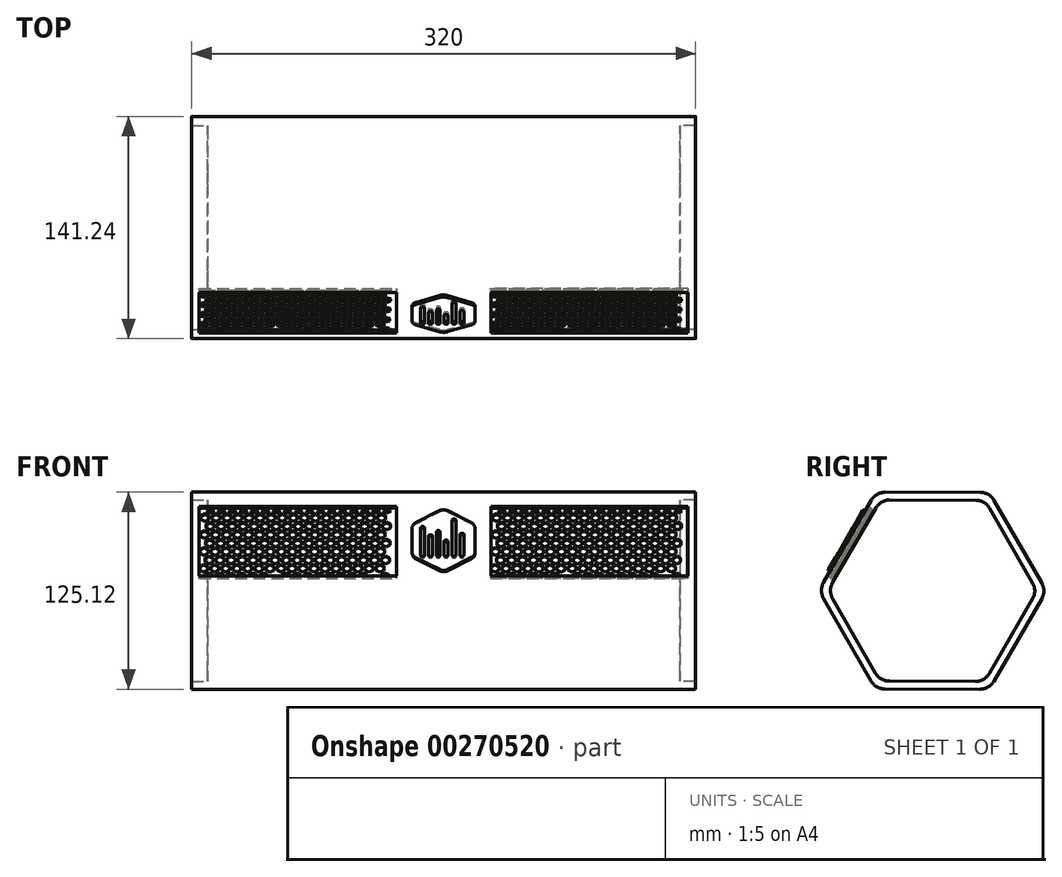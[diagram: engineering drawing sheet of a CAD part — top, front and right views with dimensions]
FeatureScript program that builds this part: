
annotation { "Feature Type Name" : "Feature", "Feature Type Description" : "" }
export const myFeature = defineFeature(function(context is Context, id is Id, definition is map)
    precondition{}
    {
        {
            var Q0;
            Q0=qCreatedBy(makeId("Right.planeOp"),FACE);
            var sketch = newSketch(context, id + "F0", { "sketchPlane" : qUnion([Q0])});
            skCircle(sketch, "E0.cCircle", {"center": v(0, 0) * mm, "radius": 62.5 * mm, "construction": true});
            skLineSegment(sketch, "E0.0", {"start": v(-72.17, 0.15) * mm, "end": v(-35.96, 62.57) * mm});
            skLineSegment(sketch, "E0.1", {"start": v(-35.96, 62.57) * mm, "end": v(36.21, 62.43) * mm});
            skLineSegment(sketch, "E0.2", {"start": v(36.21, 62.43) * mm, "end": v(72.17, -0.15) * mm});
            skLineSegment(sketch, "E0.3", {"start": v(72.17, -0.15) * mm, "end": v(35.96, -62.57) * mm});
            skLineSegment(sketch, "E0.4", {"start": v(35.96, -62.57) * mm, "end": v(-36.21, -62.43) * mm});
            skLineSegment(sketch, "E0.5", {"start": v(-36.21, -62.43) * mm, "end": v(-72.17, 0.15) * mm});
            skPoint(sketch, "E0.0.midPoint", {"position": v(-54.06, 31.36) * mm});
            skSolve(sketch);
        }
        {
            var Q0;
            Q0=makeQuery(id+"F0.imprint","IMPRINT",FACE,{"disambiguationData":[TD([[makeQuery(id+"F0.imprint","IMPRINT",EDGE,{"derivedFrom":sQuery(id+"F0.wireOp",EDGE,"E0.0")}),-1.0]])]});
            extrude(context, id + "F1", {"entities" : qUnion([Q0]), "depth" : 320 * mm});
        }
        {
            var Q0;
            Q0=makeQuery(id+"F1.opExtrude","SWEPT_FACE",FACE,{"disambiguationData":[OSD([sQuery(id+"F0.wireOp",EDGE,"E0.0")])]});
            var sketch = newSketch(context, id + "F2", { "sketchPlane" : qUnion([Q0])});
            skLineSegment(sketch, "E1", {"start": v(0, 0) * mm, "end": v(320, 0) * mm, "construction": true});
            skLineSegment(sketch, "E2", {"start": v(160, 36.08) * mm, "end": v(160, -36.08) * mm, "construction": true});
            skCircle(sketch, "E3.cCircle", {"center": v(160, 0) * mm, "radius": 19.98 * mm, "construction": true});
            skLineSegment(sketch, "E3.0", {"start": v(139.95, 11.4) * mm, "end": v(159.86, 23.07) * mm});
            skLineSegment(sketch, "E3.1", {"start": v(159.86, 23.07) * mm, "end": v(179.9, 11.66) * mm});
            skLineSegment(sketch, "E3.2", {"start": v(179.9, 11.66) * mm, "end": v(180.05, -11.4) * mm});
            skLineSegment(sketch, "E3.3", {"start": v(180.05, -11.4) * mm, "end": v(160.14, -23.07) * mm});
            skLineSegment(sketch, "E3.4", {"start": v(160.14, -23.07) * mm, "end": v(140.1, -11.66) * mm});
            skLineSegment(sketch, "E3.5", {"start": v(140.1, -11.66) * mm, "end": v(139.95, 11.4) * mm});
            skPoint(sketch, "E3.0.midPoint", {"position": v(149.9, 17.24) * mm});
            skSolve(sketch);
        }
        {
            var Q0;
            Q0=makeQuery(id+"F2.imprint","IMPRINT",FACE,{"disambiguationData":[TD([[makeQuery(id+"F2.imprint","IMPRINT",EDGE,{"derivedFrom":sQuery(id+"F2.wireOp",EDGE,"E3.0")}),-1.0]])]});
            extrude(context, id + "F3", {"entities" : qUnion([Q0]), "depth" : 1.5 * mm});
        }
        {
            var Q0;
            Q0=makeQuery(id+"F1.opExtrude","SWEPT_EDGE",EDGE,{"disambiguationData":[OSD([sQuery(id+"F0.wireOp",EDGE,"E0.1"),sQuery(id+"F0.wireOp",EDGE,"E0.2")])]});
            var Q1;
            Q1=makeQuery(id+"F1.opExtrude","SWEPT_EDGE",EDGE,{"disambiguationData":[OSD([sQuery(id+"F0.wireOp",EDGE,"E0.0"),sQuery(id+"F0.wireOp",EDGE,"E0.1")])]});
            var Q2;
            Q2=makeQuery(id+"F1.opExtrude","SWEPT_EDGE",EDGE,{"disambiguationData":[OSD([sQuery(id+"F0.wireOp",EDGE,"E0.0"),sQuery(id+"F0.wireOp",EDGE,"E0.5")])]});
            var Q3;
            Q3=makeQuery(id+"F1.opExtrude","SWEPT_EDGE",EDGE,{"disambiguationData":[OSD([sQuery(id+"F0.wireOp",EDGE,"E0.4"),sQuery(id+"F0.wireOp",EDGE,"E0.5")])]});
            var Q4;
            Q4=makeQuery(id+"F1.opExtrude","SWEPT_EDGE",EDGE,{"disambiguationData":[OSD([sQuery(id+"F0.wireOp",EDGE,"E0.3"),sQuery(id+"F0.wireOp",EDGE,"E0.4")])]});
            var Q5;
            Q5=makeQuery(id+"F1.opExtrude","SWEPT_EDGE",EDGE,{"disambiguationData":[OSD([sQuery(id+"F0.wireOp",EDGE,"E0.2"),sQuery(id+"F0.wireOp",EDGE,"E0.3")])]});
            fillet(context, id + "F4", {"entities" : qUnion([Q0, Q1, Q2, Q3, Q4, Q5]), "radius" : 10 * mm, "tangentPropagation" : true, "allowEdgeOverflow" : false});
        }
        {
            var Q0;
            Q0=makeQuery(id+"F1.opExtrude","CAP_FACE",FACE,{"disambiguationData":[OSD([sQuery(id+"F0.wireOp",EDGE,"E0.0"),sQuery(id+"F0.wireOp",EDGE,"E0.1"),sQuery(id+"F0.wireOp",EDGE,"E0.2"),sQuery(id+"F0.wireOp",EDGE,"E0.3"),sQuery(id+"F0.wireOp",EDGE,"E0.4"),sQuery(id+"F0.wireOp",EDGE,"E0.5")])],"isStart":true});
            var sketch = newSketch(context, id + "F5", { "sketchPlane" : qUnion([Q0])});
            skLineSegment(sketch, "E4", {"start": v(0, 62.5) * mm, "end": v(0.01, 57.5) * mm, "construction": true});
            skCircle(sketch, "E5.cCircle", {"center": v(0, 0) * mm, "radius": 57.5 * mm, "construction": true});
            skLineSegment(sketch, "E5.0", {"start": v(-33.19, 57.5) * mm, "end": v(33.2, 57.5) * mm});
            skLineSegment(sketch, "E5.1", {"start": v(33.2, 57.5) * mm, "end": v(66.4, -0.01) * mm});
            skLineSegment(sketch, "E5.2", {"start": v(66.4, -0.01) * mm, "end": v(33.19, -57.5) * mm});
            skLineSegment(sketch, "E5.3", {"start": v(33.19, -57.5) * mm, "end": v(-33.2, -57.5) * mm});
            skLineSegment(sketch, "E5.4", {"start": v(-33.2, -57.5) * mm, "end": v(-66.4, 0.01) * mm});
            skLineSegment(sketch, "E5.5", {"start": v(-66.4, 0.01) * mm, "end": v(-33.19, 57.5) * mm});
            skPoint(sketch, "E5.0.midPoint", {"position": v(0.01, 57.5) * mm});
            skSolve(sketch);
        }
        {
            var Q0;
            Q0=makeQuery(id+"F5.imprint","IMPRINT",FACE,{"disambiguationData":[TD([[makeQuery(id+"F5.imprint","IMPRINT",EDGE,{"derivedFrom":sQuery(id+"F5.wireOp",EDGE,"E5.0")}),-1.0]])]});
            extrude(context, id + "F6", {"entities" : qUnion([Q0]), "operationType" : NewBodyOperationType.REMOVE, "oppositeDirection" : true, "depth" : 10 * mm});
        }
        {
            var Q0;
            Q0=makeQuery(id+"F1.opExtrude","CAP_FACE",FACE,{"disambiguationData":[OSD([sQuery(id+"F0.wireOp",EDGE,"E0.0"),sQuery(id+"F0.wireOp",EDGE,"E0.1"),sQuery(id+"F0.wireOp",EDGE,"E0.2"),sQuery(id+"F0.wireOp",EDGE,"E0.3"),sQuery(id+"F0.wireOp",EDGE,"E0.4"),sQuery(id+"F0.wireOp",EDGE,"E0.5")])],"isStart":false});
            var sketch = newSketch(context, id + "F7", { "sketchPlane" : qUnion([Q0])});
            skLineSegment(sketch, "E6", {"start": v(0.13, 62.5) * mm, "end": v(0.13, 57.5) * mm, "construction": true});
            skCircle(sketch, "E7.cCircle", {"center": v(0, 0) * mm, "radius": 57.5 * mm, "construction": true});
            skLineSegment(sketch, "E7.0", {"start": v(-33.07, 57.57) * mm, "end": v(33.33, 57.43) * mm});
            skLineSegment(sketch, "E7.1", {"start": v(33.33, 57.43) * mm, "end": v(66.4, -0.15) * mm});
            skLineSegment(sketch, "E7.2", {"start": v(66.4, -0.15) * mm, "end": v(33.07, -57.57) * mm});
            skLineSegment(sketch, "E7.3", {"start": v(33.07, -57.57) * mm, "end": v(-33.33, -57.43) * mm});
            skLineSegment(sketch, "E7.4", {"start": v(-33.33, -57.43) * mm, "end": v(-66.4, 0.15) * mm});
            skLineSegment(sketch, "E7.5", {"start": v(-66.4, 0.15) * mm, "end": v(-33.07, 57.57) * mm});
            skPoint(sketch, "E7.0.midPoint", {"position": v(0.13, 57.5) * mm});
            skSolve(sketch);
        }
        {
            var Q0;
            Q0=makeQuery(id+"F7.imprint","IMPRINT",FACE,{"disambiguationData":[TD([[makeQuery(id+"F7.imprint","IMPRINT",EDGE,{"derivedFrom":sQuery(id+"F7.wireOp",EDGE,"E7.0")}),-1.0]])]});
            extrude(context, id + "F8", {"entities" : qUnion([Q0]), "operationType" : NewBodyOperationType.REMOVE, "oppositeDirection" : true, "depth" : 10 * mm});
        }
        {
            var Q0;
            Q0=makeQuery(id+"F6.boolean.opBoolean","COPY",EDGE,{"derivedFrom":makeQuery(id+"F6.opExtrude","SWEPT_EDGE",EDGE,{"disambiguationData":[OSD([sQuery(id+"F5.wireOp",EDGE,"E5.0"),sQuery(id+"F5.wireOp",EDGE,"E5.5")])]})});
            var Q1;
            Q1=makeQuery(id+"F6.boolean.opBoolean","COPY",EDGE,{"derivedFrom":makeQuery(id+"F6.opExtrude","SWEPT_EDGE",EDGE,{"disambiguationData":[OSD([sQuery(id+"F5.wireOp",EDGE,"E5.4"),sQuery(id+"F5.wireOp",EDGE,"E5.5")])]})});
            var Q2;
            Q2=makeQuery(id+"F6.boolean.opBoolean","COPY",EDGE,{"derivedFrom":makeQuery(id+"F6.opExtrude","SWEPT_EDGE",EDGE,{"disambiguationData":[OSD([sQuery(id+"F5.wireOp",EDGE,"E5.0"),sQuery(id+"F5.wireOp",EDGE,"E5.1")])]})});
            var Q3;
            Q3=makeQuery(id+"F6.boolean.opBoolean","COPY",EDGE,{"derivedFrom":makeQuery(id+"F6.opExtrude","SWEPT_EDGE",EDGE,{"disambiguationData":[OSD([sQuery(id+"F5.wireOp",EDGE,"E5.1"),sQuery(id+"F5.wireOp",EDGE,"E5.2")])]})});
            var Q4;
            Q4=makeQuery(id+"F6.boolean.opBoolean","COPY",EDGE,{"derivedFrom":makeQuery(id+"F6.opExtrude","SWEPT_EDGE",EDGE,{"disambiguationData":[OSD([sQuery(id+"F5.wireOp",EDGE,"E5.2"),sQuery(id+"F5.wireOp",EDGE,"E5.3")])]})});
            var Q5;
            Q5=makeQuery(id+"F6.boolean.opBoolean","COPY",EDGE,{"derivedFrom":makeQuery(id+"F6.opExtrude","SWEPT_EDGE",EDGE,{"disambiguationData":[OSD([sQuery(id+"F5.wireOp",EDGE,"E5.3"),sQuery(id+"F5.wireOp",EDGE,"E5.4")])]})});
            var Q6;
            Q6=makeQuery(id+"F8.boolean.opBoolean","COPY",EDGE,{"derivedFrom":makeQuery(id+"F8.opExtrude","SWEPT_EDGE",EDGE,{"disambiguationData":[OSD([sQuery(id+"F7.wireOp",EDGE,"E7.0"),sQuery(id+"F7.wireOp",EDGE,"E7.1")])]})});
            var Q7;
            Q7=makeQuery(id+"F8.boolean.opBoolean","COPY",EDGE,{"derivedFrom":makeQuery(id+"F8.opExtrude","SWEPT_EDGE",EDGE,{"disambiguationData":[OSD([sQuery(id+"F7.wireOp",EDGE,"E7.1"),sQuery(id+"F7.wireOp",EDGE,"E7.2")])]})});
            var Q8;
            Q8=makeQuery(id+"F8.boolean.opBoolean","COPY",EDGE,{"derivedFrom":makeQuery(id+"F8.opExtrude","SWEPT_EDGE",EDGE,{"disambiguationData":[OSD([sQuery(id+"F7.wireOp",EDGE,"E7.0"),sQuery(id+"F7.wireOp",EDGE,"E7.5")])]})});
            var Q9;
            Q9=makeQuery(id+"F8.boolean.opBoolean","COPY",EDGE,{"derivedFrom":makeQuery(id+"F8.opExtrude","SWEPT_EDGE",EDGE,{"disambiguationData":[OSD([sQuery(id+"F7.wireOp",EDGE,"E7.4"),sQuery(id+"F7.wireOp",EDGE,"E7.5")])]})});
            var Q10;
            Q10=makeQuery(id+"F8.boolean.opBoolean","COPY",EDGE,{"derivedFrom":makeQuery(id+"F8.opExtrude","SWEPT_EDGE",EDGE,{"disambiguationData":[OSD([sQuery(id+"F7.wireOp",EDGE,"E7.3"),sQuery(id+"F7.wireOp",EDGE,"E7.4")])]})});
            var Q11;
            Q11=makeQuery(id+"F8.boolean.opBoolean","COPY",EDGE,{"derivedFrom":makeQuery(id+"F8.opExtrude","SWEPT_EDGE",EDGE,{"disambiguationData":[OSD([sQuery(id+"F7.wireOp",EDGE,"E7.2"),sQuery(id+"F7.wireOp",EDGE,"E7.3")])]})});
            fillet(context, id + "F9", {"entities" : qUnion([Q0, Q1, Q2, Q3, Q4, Q5, Q6, Q7, Q8, Q9, Q10, Q11]), "radius" : 10 * mm, "tangentPropagation" : true, "allowEdgeOverflow" : false});
        }
        {
            var Q0;
            Q0=makeQuery(id+"F3.opExtrude","SWEPT_EDGE",EDGE,{"disambiguationData":[OSD([sQuery(id+"F2.wireOp",EDGE,"E3.0"),sQuery(id+"F2.wireOp",EDGE,"E3.1")])]});
            var Q1;
            Q1=makeQuery(id+"F3.opExtrude","SWEPT_EDGE",EDGE,{"disambiguationData":[OSD([sQuery(id+"F2.wireOp",EDGE,"E3.1"),sQuery(id+"F2.wireOp",EDGE,"E3.2")])]});
            var Q2;
            Q2=makeQuery(id+"F3.opExtrude","SWEPT_EDGE",EDGE,{"disambiguationData":[OSD([sQuery(id+"F2.wireOp",EDGE,"E3.2"),sQuery(id+"F2.wireOp",EDGE,"E3.3")])]});
            var Q3;
            Q3=makeQuery(id+"F3.opExtrude","SWEPT_EDGE",EDGE,{"disambiguationData":[OSD([sQuery(id+"F2.wireOp",EDGE,"E3.3"),sQuery(id+"F2.wireOp",EDGE,"E3.4")])]});
            var Q4;
            Q4=makeQuery(id+"F3.opExtrude","SWEPT_EDGE",EDGE,{"disambiguationData":[OSD([sQuery(id+"F2.wireOp",EDGE,"E3.4"),sQuery(id+"F2.wireOp",EDGE,"E3.5")])]});
            var Q5;
            Q5=makeQuery(id+"F3.opExtrude","SWEPT_EDGE",EDGE,{"disambiguationData":[OSD([sQuery(id+"F2.wireOp",EDGE,"E3.0"),sQuery(id+"F2.wireOp",EDGE,"E3.5")])]});
            fillet(context, id + "F10", {"entities" : qUnion([Q0, Q1, Q2, Q3, Q4, Q5]), "radius" : 5 * mm, "tangentPropagation" : true, "allowEdgeOverflow" : false});
        }
        {
            var Q0;
            Q0=makeQuery(id+"F2.imprint","IMPRINT",FACE,{"disambiguationData":[TD([[makeQuery(id+"F2.imprint","IMPRINT",EDGE,{"derivedFrom":sQuery(id+"F2.wireOp",EDGE,"E3.0")}),1.0]])]});
            var sketch = newSketch(context, id + "F11", { "sketchPlane" : qUnion([Q0])});
            skLineSegment(sketch, "E8.bottom", {"start": v(4.75, 25.56) * mm, "end": v(130, 25.56) * mm});
            skLineSegment(sketch, "E8.top", {"start": v(4.75, -25.56) * mm, "end": v(130, -25.56) * mm});
            skLineSegment(sketch, "E8.left", {"start": v(4.75, 25.56) * mm, "end": v(4.75, -25.56) * mm});
            skLineSegment(sketch, "E8.right", {"start": v(130, 25.56) * mm, "end": v(130, -25.56) * mm});
            skLineSegment(sketch, "E9.MirrorCS", {"start": v(315.25, 25.56) * mm, "end": v(190, 25.56) * mm});
            skLineSegment(sketch, "E10.MirrorCS", {"start": v(315.25, 25.56) * mm, "end": v(315.25, -25.56) * mm});
            skLineSegment(sketch, "E11.MirrorCS", {"start": v(315.25, -25.56) * mm, "end": v(190, -25.56) * mm});
            skLineSegment(sketch, "E12.MirrorCS", {"start": v(190, 25.56) * mm, "end": v(190, -25.56) * mm});
            skSolve(sketch);
        }
        {
            var Q0;
            Q0=makeQuery(id+"F11.imprint","IMPRINT",FACE,{"disambiguationData":[TD([[makeQuery(id+"F11.imprint","IMPRINT",EDGE,{"derivedFrom":sQuery(id+"F11.wireOp",EDGE,"E8.bottom")}),-1.0]])]});
            extrude(context, id + "F12", {"entities" : qUnion([Q0]), "operationType" : NewBodyOperationType.REMOVE, "oppositeDirection" : true, "depth" : 3 * mm});
        }
        {
            var Q0;
            Q0=makeQuery(id+"F11.imprint","IMPRINT",FACE,{"disambiguationData":[TD([[makeQuery(id+"F11.imprint","IMPRINT",EDGE,{"derivedFrom":sQuery(id+"F11.wireOp",EDGE,"E9.MirrorCS")}),1.0]])]});
            extrude(context, id + "F13", {"entities" : qUnion([Q0]), "operationType" : NewBodyOperationType.REMOVE, "oppositeDirection" : true, "depth" : 3 * mm});
        }
        {
            var Q0;
            Q0=makeQuery(id+"F12.boolean.opBoolean","COPY",FACE,{"derivedFrom":makeQuery(id+"F12.opExtrude","CAP_FACE",FACE,{"disambiguationData":[OSD([sQuery(id+"F11.wireOp",EDGE,"E8.bottom"),sQuery(id+"F11.wireOp",EDGE,"E8.top"),sQuery(id+"F11.wireOp",EDGE,"E8.left"),sQuery(id+"F11.wireOp",EDGE,"E8.right")])],"isStart":false})});
            extrude(context, id + "F14", {"entities" : qUnion([Q0]), "depth" : 1 * mm});
        }
        {
            var Q0;
            Q0=makeQuery(id+"F14.opExtrude","CAP_FACE",FACE,{"disambiguationData":[OSD([sQuery(id+"F11.wireOp",EDGE,"E8.bottom"),sQuery(id+"F11.wireOp",EDGE,"E8.top"),sQuery(id+"F11.wireOp",EDGE,"E8.left"),sQuery(id+"F11.wireOp",EDGE,"E8.right")])],"isStart":false});
            var sketch = newSketch(context, id + "F15", { "sketchPlane" : qUnion([Q0])});
            skLineSegment(sketch, "E13", {"start": v(67.38, 25.56) * mm, "end": v(67.38, -25.56) * mm, "construction": true});
            skCircle(sketch, "E14.cCircle", {"center": v(67.38, 0) * mm, "radius": 2.5 * mm, "construction": true});
            skLineSegment(sketch, "E14.0", {"start": v(69.87, 1.44) * mm, "end": v(69.88, -1.44) * mm});
            skLineSegment(sketch, "E14.1", {"start": v(69.87, -1.44) * mm, "end": v(67.38, -2.89) * mm});
            skLineSegment(sketch, "E14.2", {"start": v(67.38, -2.89) * mm, "end": v(64.88, -1.44) * mm});
            skLineSegment(sketch, "E14.3", {"start": v(64.88, -1.44) * mm, "end": v(64.87, 1.44) * mm});
            skLineSegment(sketch, "E14.4", {"start": v(64.88, 1.44) * mm, "end": v(67.37, 2.89) * mm});
            skLineSegment(sketch, "E14.5", {"start": v(67.37, 2.89) * mm, "end": v(69.87, 1.44) * mm});
            skCircle(sketch, "E15.cCircle", {"center": v(74.37, 0) * mm, "radius": 2.5 * mm, "construction": true});
            skLineSegment(sketch, "E15.0", {"start": v(71.85, 1.4) * mm, "end": v(74.32, 2.89) * mm});
            skLineSegment(sketch, "E15.1", {"start": v(74.32, 2.89) * mm, "end": v(76.85, 1.5) * mm});
            skLineSegment(sketch, "E15.2", {"start": v(76.85, 1.5) * mm, "end": v(76.9, -1.4) * mm});
            skLineSegment(sketch, "E15.3", {"start": v(76.9, -1.4) * mm, "end": v(74.43, -2.89) * mm});
            skLineSegment(sketch, "E15.4", {"start": v(74.43, -2.89) * mm, "end": v(71.9, -1.5) * mm});
            skLineSegment(sketch, "E15.5", {"start": v(71.9, -1.5) * mm, "end": v(71.85, 1.4) * mm});
            skCircle(sketch, "E16.cCircle", {"center": v(81.37, 0) * mm, "radius": 2.5 * mm, "construction": true});
            skLineSegment(sketch, "E16.0", {"start": v(78.87, 1.44) * mm, "end": v(81.37, 2.89) * mm});
            skLineSegment(sketch, "E16.1", {"start": v(81.37, 2.89) * mm, "end": v(83.87, 1.44) * mm});
            skLineSegment(sketch, "E16.2", {"start": v(83.87, 1.44) * mm, "end": v(83.87, -1.44) * mm});
            skLineSegment(sketch, "E16.3", {"start": v(83.87, -1.44) * mm, "end": v(81.37, -2.89) * mm});
            skLineSegment(sketch, "E16.4", {"start": v(81.37, -2.89) * mm, "end": v(78.87, -1.44) * mm});
            skLineSegment(sketch, "E16.5", {"start": v(78.87, -1.44) * mm, "end": v(78.87, 1.44) * mm});
            skCircle(sketch, "E17.cCircle", {"center": v(88.37, 0) * mm, "radius": 2.5 * mm, "construction": true});
            skLineSegment(sketch, "E17.0", {"start": v(85.87, 1.44) * mm, "end": v(88.37, 2.89) * mm});
            skLineSegment(sketch, "E17.1", {"start": v(88.37, 2.89) * mm, "end": v(90.87, 1.44) * mm});
            skLineSegment(sketch, "E17.2", {"start": v(90.87, 1.44) * mm, "end": v(90.87, -1.44) * mm});
            skLineSegment(sketch, "E17.3", {"start": v(90.87, -1.44) * mm, "end": v(88.37, -2.89) * mm});
            skLineSegment(sketch, "E17.4", {"start": v(88.37, -2.89) * mm, "end": v(85.87, -1.44) * mm});
            skLineSegment(sketch, "E17.5", {"start": v(85.87, -1.44) * mm, "end": v(85.87, 1.44) * mm});
            skCircle(sketch, "E18.cCircle", {"center": v(95.37, 0) * mm, "radius": 2.5 * mm, "construction": true});
            skLineSegment(sketch, "E18.0", {"start": v(92.87, 1.44) * mm, "end": v(95.37, 2.89) * mm});
            skLineSegment(sketch, "E18.1", {"start": v(95.37, 2.89) * mm, "end": v(97.87, 1.44) * mm});
            skLineSegment(sketch, "E18.2", {"start": v(97.87, 1.44) * mm, "end": v(97.87, -1.44) * mm});
            skLineSegment(sketch, "E18.3", {"start": v(97.87, -1.44) * mm, "end": v(95.37, -2.89) * mm});
            skLineSegment(sketch, "E18.4", {"start": v(95.37, -2.89) * mm, "end": v(92.87, -1.44) * mm});
            skLineSegment(sketch, "E18.5", {"start": v(92.87, -1.44) * mm, "end": v(92.87, 1.44) * mm});
            skCircle(sketch, "E19.cCircle", {"center": v(102.38, 0) * mm, "radius": 2.5 * mm, "construction": true});
            skLineSegment(sketch, "E19.0", {"start": v(99.88, 1.44) * mm, "end": v(102.38, 2.89) * mm});
            skLineSegment(sketch, "E19.1", {"start": v(102.38, 2.89) * mm, "end": v(104.88, 1.44) * mm});
            skLineSegment(sketch, "E19.2", {"start": v(104.88, 1.44) * mm, "end": v(104.88, -1.44) * mm});
            skLineSegment(sketch, "E19.3", {"start": v(104.88, -1.44) * mm, "end": v(102.38, -2.89) * mm});
            skLineSegment(sketch, "E19.4", {"start": v(102.38, -2.89) * mm, "end": v(99.88, -1.44) * mm});
            skLineSegment(sketch, "E19.5", {"start": v(99.88, -1.44) * mm, "end": v(99.88, 1.44) * mm});
            skCircle(sketch, "E20.cCircle", {"center": v(109.38, 0) * mm, "radius": 2.5 * mm, "construction": true});
            skLineSegment(sketch, "E20.0", {"start": v(106.88, 1.44) * mm, "end": v(109.38, 2.89) * mm});
            skLineSegment(sketch, "E20.1", {"start": v(109.38, 2.89) * mm, "end": v(111.88, 1.44) * mm});
            skLineSegment(sketch, "E20.2", {"start": v(111.88, 1.44) * mm, "end": v(111.88, -1.44) * mm});
            skLineSegment(sketch, "E20.3", {"start": v(111.88, -1.44) * mm, "end": v(109.38, -2.89) * mm});
            skLineSegment(sketch, "E20.4", {"start": v(109.38, -2.89) * mm, "end": v(106.88, -1.44) * mm});
            skLineSegment(sketch, "E20.5", {"start": v(106.88, -1.44) * mm, "end": v(106.88, 1.44) * mm});
            skCircle(sketch, "E21.cCircle", {"center": v(116.38, 0) * mm, "radius": 2.5 * mm, "construction": true});
            skLineSegment(sketch, "E21.0", {"start": v(113.88, 1.44) * mm, "end": v(116.38, 2.89) * mm});
            skLineSegment(sketch, "E21.1", {"start": v(116.38, 2.89) * mm, "end": v(118.88, 1.44) * mm});
            skLineSegment(sketch, "E21.2", {"start": v(118.88, 1.44) * mm, "end": v(118.88, -1.44) * mm});
            skLineSegment(sketch, "E21.3", {"start": v(118.88, -1.44) * mm, "end": v(116.38, -2.89) * mm});
            skLineSegment(sketch, "E21.4", {"start": v(116.38, -2.89) * mm, "end": v(113.88, -1.44) * mm});
            skLineSegment(sketch, "E21.5", {"start": v(113.88, -1.44) * mm, "end": v(113.88, 1.44) * mm});
            skCircle(sketch, "E22.cCircle", {"center": v(123.37, 0) * mm, "radius": 2.5 * mm, "construction": true});
            skLineSegment(sketch, "E22.0", {"start": v(120.88, 1.44) * mm, "end": v(123.38, 2.89) * mm});
            skLineSegment(sketch, "E22.1", {"start": v(123.38, 2.89) * mm, "end": v(125.88, 1.44) * mm});
            skLineSegment(sketch, "E22.2", {"start": v(125.88, 1.44) * mm, "end": v(125.87, -1.44) * mm});
            skLineSegment(sketch, "E22.3", {"start": v(125.87, -1.44) * mm, "end": v(123.37, -2.89) * mm});
            skLineSegment(sketch, "E22.4", {"start": v(123.37, -2.89) * mm, "end": v(120.87, -1.44) * mm});
            skLineSegment(sketch, "E22.5", {"start": v(120.87, -1.44) * mm, "end": v(120.88, 1.44) * mm});
            skLineSegment(sketch, "E23.MirrorCS", {"start": v(25.37, -2.89) * mm, "end": v(27.87, -1.44) * mm});
            skLineSegment(sketch, "E24.MirrorCS", {"start": v(20.87, 1.44) * mm, "end": v(18.37, 2.89) * mm});
            skLineSegment(sketch, "E25.MirrorCS", {"start": v(18.37, -2.89) * mm, "end": v(20.87, -1.44) * mm});
            skLineSegment(sketch, "E26.MirrorCS", {"start": v(32.37, -2.89) * mm, "end": v(34.87, -1.44) * mm});
            skLineSegment(sketch, "E27.MirrorCS", {"start": v(11.37, 2.89) * mm, "end": v(8.87, 1.44) * mm});
            skLineSegment(sketch, "E28.MirrorCS", {"start": v(46.38, 2.89) * mm, "end": v(43.88, 1.44) * mm});
            skCircle(sketch, "E29.MirrorC", {"center": v(25.37, 0) * mm, "radius": 2.5 * mm, "construction": true});
            skLineSegment(sketch, "E30.MirrorCS", {"start": v(18.37, 2.89) * mm, "end": v(15.87, 1.44) * mm});
            skLineSegment(sketch, "E31.MirrorCS", {"start": v(8.88, -1.44) * mm, "end": v(11.38, -2.89) * mm});
            skLineSegment(sketch, "E32.MirrorCS", {"start": v(27.87, 1.44) * mm, "end": v(25.37, 2.89) * mm});
            skLineSegment(sketch, "E33.MirrorCS", {"start": v(13.87, 1.44) * mm, "end": v(11.37, 2.89) * mm});
            skLineSegment(sketch, "E34.MirrorCS", {"start": v(34.87, 1.44) * mm, "end": v(32.37, 2.89) * mm});
            skLineSegment(sketch, "E35.MirrorCS", {"start": v(20.87, -1.44) * mm, "end": v(20.87, 1.44) * mm});
            skLineSegment(sketch, "E36.MirrorCS", {"start": v(29.87, 1.44) * mm, "end": v(29.87, -1.44) * mm});
            skLineSegment(sketch, "E37.MirrorCS", {"start": v(11.38, -2.89) * mm, "end": v(13.88, -1.44) * mm});
            skLineSegment(sketch, "E38.MirrorCS", {"start": v(15.87, -1.44) * mm, "end": v(18.37, -2.89) * mm});
            skLineSegment(sketch, "E39.MirrorCS", {"start": v(8.87, 1.44) * mm, "end": v(8.88, -1.44) * mm});
            skLineSegment(sketch, "E40.MirrorCS", {"start": v(53.38, -2.89) * mm, "end": v(55.88, -1.44) * mm});
            skLineSegment(sketch, "E41.MirrorCS", {"start": v(55.88, 1.44) * mm, "end": v(53.38, 2.89) * mm});
            skLineSegment(sketch, "E42.MirrorCS", {"start": v(22.87, -1.44) * mm, "end": v(25.37, -2.89) * mm});
            skCircle(sketch, "E43.MirrorC", {"center": v(18.37, 0) * mm, "radius": 2.5 * mm, "construction": true});
            skLineSegment(sketch, "E44.MirrorCS", {"start": v(41.88, 1.44) * mm, "end": v(39.38, 2.89) * mm});
            skLineSegment(sketch, "E45.MirrorCS", {"start": v(34.87, -1.44) * mm, "end": v(34.87, 1.44) * mm});
            skCircle(sketch, "E46.MirrorC", {"center": v(11.38, 0) * mm, "radius": 2.5 * mm, "construction": true});
            skLineSegment(sketch, "E47.MirrorCS", {"start": v(53.38, 2.89) * mm, "end": v(50.88, 1.44) * mm});
            skLineSegment(sketch, "E48.MirrorCS", {"start": v(32.37, 2.89) * mm, "end": v(29.87, 1.44) * mm});
            skLineSegment(sketch, "E49.MirrorCS", {"start": v(50.88, -1.44) * mm, "end": v(53.38, -2.89) * mm});
            skCircle(sketch, "E50.MirrorC", {"center": v(32.37, 0) * mm, "radius": 2.5 * mm, "construction": true});
            skLineSegment(sketch, "E51.MirrorCS", {"start": v(46.38, -2.89) * mm, "end": v(48.88, -1.44) * mm});
            skLineSegment(sketch, "E52.MirrorCS", {"start": v(48.88, 1.44) * mm, "end": v(46.38, 2.89) * mm});
            skLineSegment(sketch, "E53.MirrorCS", {"start": v(13.88, -1.44) * mm, "end": v(13.87, 1.44) * mm});
            skLineSegment(sketch, "E54.MirrorCS", {"start": v(39.38, 2.89) * mm, "end": v(36.88, 1.44) * mm});
            skLineSegment(sketch, "E55.MirrorCS", {"start": v(43.88, -1.44) * mm, "end": v(46.38, -2.89) * mm});
            skLineSegment(sketch, "E56.MirrorCS", {"start": v(29.87, -1.44) * mm, "end": v(32.37, -2.89) * mm});
            skLineSegment(sketch, "E57.MirrorCS", {"start": v(36.88, -1.44) * mm, "end": v(39.38, -2.89) * mm});
            skLineSegment(sketch, "E58.MirrorCS", {"start": v(39.38, -2.89) * mm, "end": v(41.88, -1.44) * mm});
            skLineSegment(sketch, "E59.MirrorCS", {"start": v(25.37, 2.89) * mm, "end": v(22.87, 1.44) * mm});
            skLineSegment(sketch, "E60.MirrorCS", {"start": v(22.87, 1.44) * mm, "end": v(22.87, -1.44) * mm});
            skLineSegment(sketch, "E61.MirrorCS", {"start": v(15.87, 1.44) * mm, "end": v(15.87, -1.44) * mm});
            skLineSegment(sketch, "E62.MirrorCS", {"start": v(27.87, -1.44) * mm, "end": v(27.87, 1.44) * mm});
            skLineSegment(sketch, "E63.MirrorCS", {"start": v(55.88, -1.44) * mm, "end": v(55.88, 1.44) * mm});
            skLineSegment(sketch, "E64.MirrorCS", {"start": v(36.88, 1.44) * mm, "end": v(36.88, -1.44) * mm});
            skLineSegment(sketch, "E65.MirrorCS", {"start": v(48.88, -1.44) * mm, "end": v(48.88, 1.44) * mm});
            skLineSegment(sketch, "E66.MirrorCS", {"start": v(43.88, 1.44) * mm, "end": v(43.88, -1.44) * mm});
            skLineSegment(sketch, "E67.MirrorCS", {"start": v(50.88, 1.44) * mm, "end": v(50.88, -1.44) * mm});
            skLineSegment(sketch, "E68.MirrorCS", {"start": v(41.88, -1.44) * mm, "end": v(41.88, 1.44) * mm});
            skCircle(sketch, "E69.MirrorC", {"center": v(53.38, 0) * mm, "radius": 2.5 * mm, "construction": true});
            skCircle(sketch, "E70.MirrorC", {"center": v(39.38, 0) * mm, "radius": 2.5 * mm, "construction": true});
            skCircle(sketch, "E71.MirrorC", {"center": v(46.38, 0) * mm, "radius": 2.5 * mm, "construction": true});
            skLineSegment(sketch, "E72.MirrorCS", {"start": v(60.43, 2.89) * mm, "end": v(57.9, 1.5) * mm});
            skLineSegment(sketch, "E73.MirrorCS", {"start": v(57.85, -1.4) * mm, "end": v(60.32, -2.89) * mm});
            skLineSegment(sketch, "E74.MirrorCS", {"start": v(62.85, -1.5) * mm, "end": v(62.9, 1.4) * mm});
            skLineSegment(sketch, "E75.MirrorCS", {"start": v(62.9, 1.4) * mm, "end": v(60.43, 2.89) * mm});
            skLineSegment(sketch, "E76.MirrorCS", {"start": v(57.9, 1.5) * mm, "end": v(57.85, -1.4) * mm});
            skLineSegment(sketch, "E77.MirrorCS", {"start": v(60.32, -2.89) * mm, "end": v(62.85, -1.5) * mm});
            skCircle(sketch, "E78.MirrorC", {"center": v(60.38, 0) * mm, "radius": 2.5 * mm, "construction": true});
            skCircle(sketch, "E79.1.0.4", {"center": v(36.24, 6.26) * mm, "radius": 2.5 * mm, "construction": true});
            skCircle(sketch, "E79.1.0.5", {"center": v(85.24, 6.26) * mm, "radius": 2.5 * mm, "construction": true});
            skCircle(sketch, "E79.1.0.6", {"center": v(64.24, 6.26) * mm, "radius": 2.5 * mm, "construction": true});
            skLineSegment(sketch, "E79.1.0.7", {"start": v(47.74, 7.7) * mm, "end": v(47.74, 4.82) * mm});
            skLineSegment(sketch, "E79.1.0.8", {"start": v(103.74, 7.7) * mm, "end": v(106.24, 9.15) * mm});
            skLineSegment(sketch, "E79.1.0.9", {"start": v(8.24, 3.37) * mm, "end": v(10.74, 4.82) * mm});
            skLineSegment(sketch, "E79.1.0.10", {"start": v(120.24, 3.37) * mm, "end": v(117.74, 4.82) * mm});
            skLineSegment(sketch, "E79.1.0.11", {"start": v(19.74, 7.7) * mm, "end": v(19.74, 4.82) * mm});
            skLineSegment(sketch, "E79.1.0.12", {"start": v(10.74, 4.82) * mm, "end": v(10.74, 7.7) * mm});
            skLineSegment(sketch, "E79.1.0.13", {"start": v(38.74, 7.7) * mm, "end": v(36.24, 9.15) * mm});
            skCircle(sketch, "E79.1.0.14", {"center": v(50.24, 6.26) * mm, "radius": 2.5 * mm, "construction": true});
            skLineSegment(sketch, "E79.1.0.15", {"start": v(89.74, 7.7) * mm, "end": v(92.24, 9.15) * mm});
            skLineSegment(sketch, "E79.1.0.16", {"start": v(96.74, 7.7) * mm, "end": v(99.24, 9.15) * mm});
            skLineSegment(sketch, "E79.1.0.17", {"start": v(66.74, 4.82) * mm, "end": v(64.24, 3.37) * mm});
            skLineSegment(sketch, "E79.1.0.18", {"start": v(115.74, 7.7) * mm, "end": v(115.74, 4.82) * mm});
            skLineSegment(sketch, "E79.1.0.19", {"start": v(108.74, 7.7) * mm, "end": v(108.74, 4.82) * mm});
            skLineSegment(sketch, "E79.1.0.20", {"start": v(40.74, 7.7) * mm, "end": v(40.74, 4.82) * mm});
            skCircle(sketch, "E79.1.0.21", {"center": v(106.24, 6.26) * mm, "radius": 2.5 * mm, "construction": true});
            skCircle(sketch, "E79.1.0.22", {"center": v(29.24, 6.26) * mm, "radius": 2.5 * mm, "construction": true});
            skLineSegment(sketch, "E79.1.0.23", {"start": v(85.24, 3.37) * mm, "end": v(82.74, 4.82) * mm});
            skCircle(sketch, "E79.1.0.24", {"center": v(15.24, 6.26) * mm, "radius": 2.5 * mm, "construction": true});
            skLineSegment(sketch, "E79.1.0.25", {"start": v(78.24, 3.37) * mm, "end": v(75.74, 4.82) * mm});
            skLineSegment(sketch, "E79.1.0.26", {"start": v(8.24, 9.15) * mm, "end": v(5.74, 7.7) * mm});
            skLineSegment(sketch, "E79.1.0.27", {"start": v(122.74, 4.82) * mm, "end": v(120.24, 3.37) * mm});
            skLineSegment(sketch, "E79.1.0.28", {"start": v(64.24, 3.37) * mm, "end": v(61.74, 4.82) * mm});
            skLineSegment(sketch, "E79.1.0.29", {"start": v(45.74, 7.7) * mm, "end": v(43.24, 9.15) * mm});
            skLineSegment(sketch, "E79.1.0.30", {"start": v(113.24, 9.15) * mm, "end": v(115.74, 7.7) * mm});
            skLineSegment(sketch, "E79.1.0.31", {"start": v(59.77, 7.65) * mm, "end": v(57.3, 9.15) * mm});
            skLineSegment(sketch, "E79.1.0.32", {"start": v(38.74, 4.82) * mm, "end": v(38.74, 7.7) * mm});
            skLineSegment(sketch, "E79.1.0.33", {"start": v(106.24, 9.15) * mm, "end": v(108.74, 7.7) * mm});
            skCircle(sketch, "E79.1.0.34", {"center": v(92.24, 6.26) * mm, "radius": 2.5 * mm, "construction": true});
            skCircle(sketch, "E79.1.0.35", {"center": v(99.24, 6.26) * mm, "radius": 2.5 * mm, "construction": true});
            skLineSegment(sketch, "E79.1.0.36", {"start": v(45.74, 4.82) * mm, "end": v(45.74, 7.7) * mm});
            skLineSegment(sketch, "E79.1.0.37", {"start": v(96.74, 4.82) * mm, "end": v(96.74, 7.7) * mm});
            skLineSegment(sketch, "E79.1.0.38", {"start": v(117.74, 7.7) * mm, "end": v(120.24, 9.15) * mm});
            skLineSegment(sketch, "E79.1.0.39", {"start": v(47.74, 4.82) * mm, "end": v(50.24, 3.37) * mm});
            skLineSegment(sketch, "E79.1.0.40", {"start": v(10.74, 7.7) * mm, "end": v(8.24, 9.15) * mm});
            skLineSegment(sketch, "E79.1.0.41", {"start": v(59.71, 4.77) * mm, "end": v(59.77, 7.65) * mm});
            skLineSegment(sketch, "E79.1.0.42", {"start": v(89.74, 4.82) * mm, "end": v(89.74, 7.7) * mm});
            skLineSegment(sketch, "E79.1.0.43", {"start": v(110.74, 7.7) * mm, "end": v(113.24, 9.15) * mm});
            skLineSegment(sketch, "E79.1.0.44", {"start": v(33.74, 4.82) * mm, "end": v(36.24, 3.37) * mm});
            skLineSegment(sketch, "E79.1.0.45", {"start": v(52.74, 7.7) * mm, "end": v(50.24, 9.15) * mm});
            skLineSegment(sketch, "E79.1.0.46", {"start": v(29.24, 3.37) * mm, "end": v(31.74, 4.82) * mm});
            skLineSegment(sketch, "E79.1.0.47", {"start": v(26.74, 4.82) * mm, "end": v(29.24, 3.37) * mm});
            skLineSegment(sketch, "E79.1.0.48", {"start": v(24.74, 4.82) * mm, "end": v(24.74, 7.7) * mm});
            skLineSegment(sketch, "E79.1.0.49", {"start": v(101.74, 7.7) * mm, "end": v(101.74, 4.82) * mm});
            skCircle(sketch, "E79.1.0.50", {"center": v(57.24, 6.26) * mm, "radius": 2.5 * mm, "construction": true});
            skLineSegment(sketch, "E79.1.0.51", {"start": v(113.24, 3.37) * mm, "end": v(110.74, 4.82) * mm});
            skLineSegment(sketch, "E79.1.0.52", {"start": v(15.24, 9.15) * mm, "end": v(12.74, 7.7) * mm});
            skCircle(sketch, "E79.1.0.53", {"center": v(8.24, 6.26) * mm, "radius": 2.5 * mm, "construction": true});
            skCircle(sketch, "E79.1.0.54", {"center": v(120.24, 6.26) * mm, "radius": 2.5 * mm, "construction": true});
            skLineSegment(sketch, "E79.1.0.55", {"start": v(24.74, 7.7) * mm, "end": v(22.24, 9.15) * mm});
            skLineSegment(sketch, "E79.1.0.56", {"start": v(5.74, 7.7) * mm, "end": v(5.74, 4.82) * mm});
            skLineSegment(sketch, "E79.1.0.57", {"start": v(87.74, 7.7) * mm, "end": v(87.74, 4.82) * mm});
            skLineSegment(sketch, "E79.1.0.58", {"start": v(29.24, 9.15) * mm, "end": v(26.74, 7.7) * mm});
            skCircle(sketch, "E79.1.0.59", {"center": v(43.24, 6.26) * mm, "radius": 2.5 * mm, "construction": true});
            skLineSegment(sketch, "E79.1.0.60", {"start": v(94.74, 7.7) * mm, "end": v(94.74, 4.82) * mm});
            skLineSegment(sketch, "E79.1.0.61", {"start": v(75.74, 7.7) * mm, "end": v(78.24, 9.15) * mm});
            skLineSegment(sketch, "E79.1.0.62", {"start": v(106.24, 3.37) * mm, "end": v(103.74, 4.82) * mm});
            skLineSegment(sketch, "E79.1.0.63", {"start": v(73.77, 4.87) * mm, "end": v(71.3, 3.37) * mm});
            skLineSegment(sketch, "E79.1.0.64", {"start": v(73.71, 7.75) * mm, "end": v(73.77, 4.87) * mm});
            skLineSegment(sketch, "E79.1.0.65", {"start": v(71.19, 9.15) * mm, "end": v(73.71, 7.75) * mm});
            skLineSegment(sketch, "E79.1.0.66", {"start": v(68.71, 7.65) * mm, "end": v(71.19, 9.15) * mm});
            skCircle(sketch, "E79.1.0.67", {"center": v(71.24, 6.26) * mm, "radius": 2.5 * mm, "construction": true});
            skLineSegment(sketch, "E79.1.0.68", {"start": v(64.24, 9.15) * mm, "end": v(66.74, 7.7) * mm});
            skLineSegment(sketch, "E79.1.0.69", {"start": v(117.74, 4.82) * mm, "end": v(117.74, 7.7) * mm});
            skLineSegment(sketch, "E79.1.0.70", {"start": v(36.24, 9.15) * mm, "end": v(33.74, 7.7) * mm});
            skLineSegment(sketch, "E79.1.0.71", {"start": v(31.74, 4.82) * mm, "end": v(31.74, 7.7) * mm});
            skLineSegment(sketch, "E79.1.0.72", {"start": v(57.19, 3.37) * mm, "end": v(59.71, 4.77) * mm});
            skLineSegment(sketch, "E79.1.0.73", {"start": v(61.74, 7.7) * mm, "end": v(64.24, 9.15) * mm});
            skLineSegment(sketch, "E79.1.0.74", {"start": v(92.24, 9.15) * mm, "end": v(94.74, 7.7) * mm});
            skLineSegment(sketch, "E79.1.0.75", {"start": v(108.74, 4.82) * mm, "end": v(106.24, 3.37) * mm});
            skLineSegment(sketch, "E79.1.0.76", {"start": v(120.24, 9.15) * mm, "end": v(122.74, 7.7) * mm});
            skLineSegment(sketch, "E79.1.0.77", {"start": v(17.74, 4.82) * mm, "end": v(17.74, 7.7) * mm});
            skLineSegment(sketch, "E79.1.0.78", {"start": v(122.74, 7.7) * mm, "end": v(122.74, 4.82) * mm});
            skLineSegment(sketch, "E79.1.0.79", {"start": v(92.24, 3.37) * mm, "end": v(89.74, 4.82) * mm});
            skLineSegment(sketch, "E79.1.0.80", {"start": v(82.74, 4.82) * mm, "end": v(82.74, 7.7) * mm});
            skCircle(sketch, "E79.1.0.81", {"center": v(78.24, 6.26) * mm, "radius": 2.5 * mm, "construction": true});
            skLineSegment(sketch, "E79.1.0.82", {"start": v(68.77, 4.77) * mm, "end": v(68.71, 7.65) * mm});
            skLineSegment(sketch, "E79.1.0.83", {"start": v(71.3, 3.37) * mm, "end": v(68.77, 4.77) * mm});
            skLineSegment(sketch, "E79.1.0.84", {"start": v(50.24, 3.37) * mm, "end": v(52.74, 4.82) * mm});
            skLineSegment(sketch, "E79.1.0.85", {"start": v(103.74, 4.82) * mm, "end": v(103.74, 7.7) * mm});
            skLineSegment(sketch, "E79.1.0.86", {"start": v(82.74, 7.7) * mm, "end": v(85.24, 9.15) * mm});
            skLineSegment(sketch, "E79.1.0.87", {"start": v(22.24, 3.37) * mm, "end": v(24.74, 4.82) * mm});
            skLineSegment(sketch, "E79.1.0.88", {"start": v(40.74, 4.82) * mm, "end": v(43.24, 3.37) * mm});
            skLineSegment(sketch, "E79.1.0.89", {"start": v(54.77, 7.75) * mm, "end": v(54.71, 4.87) * mm});
            skLineSegment(sketch, "E79.1.0.90", {"start": v(80.74, 7.7) * mm, "end": v(80.74, 4.82) * mm});
            skLineSegment(sketch, "E79.1.0.91", {"start": v(75.74, 4.82) * mm, "end": v(75.74, 7.7) * mm});
            skCircle(sketch, "E79.1.0.92", {"center": v(22.24, 6.26) * mm, "radius": 2.5 * mm, "construction": true});
            skLineSegment(sketch, "E79.1.0.93", {"start": v(87.74, 4.82) * mm, "end": v(85.24, 3.37) * mm});
            skLineSegment(sketch, "E79.1.0.94", {"start": v(36.24, 3.37) * mm, "end": v(38.74, 4.82) * mm});
            skLineSegment(sketch, "E79.1.0.95", {"start": v(33.74, 7.7) * mm, "end": v(33.74, 4.82) * mm});
            skLineSegment(sketch, "E79.1.0.96", {"start": v(99.24, 3.37) * mm, "end": v(96.74, 4.82) * mm});
            skCircle(sketch, "E79.1.0.97", {"center": v(113.24, 6.26) * mm, "radius": 2.5 * mm, "construction": true});
            skLineSegment(sketch, "E79.1.0.98", {"start": v(101.74, 4.82) * mm, "end": v(99.24, 3.37) * mm});
            skLineSegment(sketch, "E79.1.0.99", {"start": v(110.74, 4.82) * mm, "end": v(110.74, 7.7) * mm});
            skLineSegment(sketch, "E79.1.0.100", {"start": v(50.24, 9.15) * mm, "end": v(47.74, 7.7) * mm});
            skLineSegment(sketch, "E79.1.0.101", {"start": v(17.74, 7.7) * mm, "end": v(15.24, 9.15) * mm});
            skLineSegment(sketch, "E79.1.0.102", {"start": v(57.3, 9.15) * mm, "end": v(54.77, 7.75) * mm});
            skLineSegment(sketch, "E79.1.0.103", {"start": v(94.74, 4.82) * mm, "end": v(92.24, 3.37) * mm});
            skLineSegment(sketch, "E79.1.0.104", {"start": v(78.24, 9.15) * mm, "end": v(80.74, 7.7) * mm});
            skLineSegment(sketch, "E79.1.0.105", {"start": v(43.24, 9.15) * mm, "end": v(40.74, 7.7) * mm});
            skLineSegment(sketch, "E79.1.0.106", {"start": v(12.74, 4.82) * mm, "end": v(15.24, 3.37) * mm});
            skLineSegment(sketch, "E79.1.0.107", {"start": v(85.24, 9.15) * mm, "end": v(87.74, 7.7) * mm});
            skLineSegment(sketch, "E79.1.0.108", {"start": v(66.74, 7.7) * mm, "end": v(66.74, 4.82) * mm});
            skLineSegment(sketch, "E79.1.0.109", {"start": v(31.74, 7.7) * mm, "end": v(29.24, 9.15) * mm});
            skLineSegment(sketch, "E79.1.0.110", {"start": v(26.74, 7.7) * mm, "end": v(26.74, 4.82) * mm});
            skLineSegment(sketch, "E79.1.0.111", {"start": v(22.24, 9.15) * mm, "end": v(19.74, 7.7) * mm});
            skLineSegment(sketch, "E79.1.0.112", {"start": v(19.74, 4.82) * mm, "end": v(22.24, 3.37) * mm});
            skLineSegment(sketch, "E79.1.0.113", {"start": v(15.24, 3.37) * mm, "end": v(17.74, 4.82) * mm});
            skLineSegment(sketch, "E79.1.0.114", {"start": v(80.74, 4.82) * mm, "end": v(78.24, 3.37) * mm});
            skLineSegment(sketch, "E79.1.0.115", {"start": v(54.71, 4.87) * mm, "end": v(57.19, 3.37) * mm});
            skLineSegment(sketch, "E79.1.0.116", {"start": v(12.74, 7.7) * mm, "end": v(12.74, 4.82) * mm});
            skLineSegment(sketch, "E79.1.0.117", {"start": v(115.74, 4.82) * mm, "end": v(113.24, 3.37) * mm});
            skLineSegment(sketch, "E79.1.0.118", {"start": v(99.24, 9.15) * mm, "end": v(101.74, 7.7) * mm});
            skLineSegment(sketch, "E79.1.0.119", {"start": v(61.74, 4.82) * mm, "end": v(61.74, 7.7) * mm});
            skLineSegment(sketch, "E79.1.0.120", {"start": v(43.24, 3.37) * mm, "end": v(45.74, 4.82) * mm});
            skLineSegment(sketch, "E79.1.0.121", {"start": v(52.74, 4.82) * mm, "end": v(52.74, 7.7) * mm});
            skLineSegment(sketch, "E79.1.0.122", {"start": v(5.74, 4.82) * mm, "end": v(8.24, 3.37) * mm});
            skLineSegment(sketch, "E79.direction1", {"start": v(8.88, -1.44) * mm, "end": v(5.74, 4.82) * mm, "construction": true});
            skLineSegment(sketch, "E80.1.0.0", {"start": v(9.2, 10.99) * mm, "end": v(6.07, 17.25) * mm, "construction": true});
            skLineSegment(sketch, "E80.1.0.1", {"start": v(126.2, 10.99) * mm, "end": v(123.7, 9.54) * mm});
            skLineSegment(sketch, "E80.1.0.2", {"start": v(30.2, 13.87) * mm, "end": v(30.2, 10.99) * mm});
            skLineSegment(sketch, "E80.1.0.3", {"start": v(119.2, 10.99) * mm, "end": v(116.7, 9.54) * mm});
            skLineSegment(sketch, "E80.1.0.4", {"start": v(29.57, 15.8) * mm, "end": v(32.07, 17.25) * mm});
            skLineSegment(sketch, "E80.1.0.5", {"start": v(56.2, 13.87) * mm, "end": v(53.7, 15.32) * mm});
            skLineSegment(sketch, "E80.1.0.6", {"start": v(21.2, 10.99) * mm, "end": v(21.2, 13.87) * mm});
            skLineSegment(sketch, "E80.1.0.7", {"start": v(51.2, 10.99) * mm, "end": v(53.7, 9.54) * mm});
            skLineSegment(sketch, "E80.1.0.8", {"start": v(91.2, 10.99) * mm, "end": v(88.7, 9.54) * mm});
            skLineSegment(sketch, "E80.1.0.9", {"start": v(20.07, 20.13) * mm, "end": v(20.07, 17.25) * mm});
            skLineSegment(sketch, "E80.1.0.10", {"start": v(123.07, 17.25) * mm, "end": v(120.57, 15.8) * mm});
            skLineSegment(sketch, "E80.1.0.11", {"start": v(27.07, 20.13) * mm, "end": v(27.07, 17.25) * mm});
            skLineSegment(sketch, "E80.1.0.12", {"start": v(121.2, 10.99) * mm, "end": v(121.2, 13.87) * mm});
            skLineSegment(sketch, "E80.1.0.13", {"start": v(25.7, 9.54) * mm, "end": v(28.2, 10.99) * mm});
            skLineSegment(sketch, "E80.1.0.14", {"start": v(22.57, 21.58) * mm, "end": v(20.07, 20.13) * mm});
            skLineSegment(sketch, "E80.1.0.15", {"start": v(123.07, 20.13) * mm, "end": v(123.07, 17.25) * mm});
            skCircle(sketch, "E80.1.0.16", {"center": v(43.57, 18.69) * mm, "radius": 2.5 * mm, "construction": true});
            skLineSegment(sketch, "E80.1.0.17", {"start": v(37.2, 10.99) * mm, "end": v(39.7, 9.54) * mm});
            skLineSegment(sketch, "E80.1.0.18", {"start": v(49.2, 13.87) * mm, "end": v(46.7, 15.32) * mm});
            skLineSegment(sketch, "E80.1.0.19", {"start": v(9.2, 13.87) * mm, "end": v(9.2, 10.99) * mm});
            skCircle(sketch, "E80.1.0.20", {"center": v(46.7, 12.43) * mm, "radius": 2.5 * mm, "construction": true});
            skLineSegment(sketch, "E80.1.0.21", {"start": v(44.2, 10.99) * mm, "end": v(46.7, 9.54) * mm});
            skLineSegment(sketch, "E80.1.0.22", {"start": v(32.07, 17.25) * mm, "end": v(32.07, 20.13) * mm});
            skLineSegment(sketch, "E80.1.0.23", {"start": v(44.2, 13.87) * mm, "end": v(44.2, 10.99) * mm});
            skLineSegment(sketch, "E80.1.0.24", {"start": v(85.57, 15.8) * mm, "end": v(83.07, 17.25) * mm});
            skLineSegment(sketch, "E80.1.0.25", {"start": v(79.2, 13.87) * mm, "end": v(81.7, 15.32) * mm});
            skLineSegment(sketch, "E80.1.0.26", {"start": v(16.2, 10.99) * mm, "end": v(18.7, 9.54) * mm});
            skLineSegment(sketch, "E80.1.0.27", {"start": v(119.2, 13.87) * mm, "end": v(119.2, 10.99) * mm});
            skCircle(sketch, "E80.1.0.28", {"center": v(18.7, 12.43) * mm, "radius": 2.5 * mm, "construction": true});
            skLineSegment(sketch, "E80.1.0.29", {"start": v(81.7, 9.54) * mm, "end": v(79.2, 10.99) * mm});
            skLineSegment(sketch, "E80.1.0.30", {"start": v(58.23, 13.92) * mm, "end": v(58.18, 11.04) * mm});
            skLineSegment(sketch, "E80.1.0.31", {"start": v(23.2, 13.87) * mm, "end": v(23.2, 10.99) * mm});
            skLineSegment(sketch, "E80.1.0.32", {"start": v(79.2, 10.99) * mm, "end": v(79.2, 13.87) * mm});
            skLineSegment(sketch, "E80.1.0.33", {"start": v(46.7, 15.32) * mm, "end": v(44.2, 13.87) * mm});
            skCircle(sketch, "E80.1.0.34", {"center": v(39.7, 12.43) * mm, "radius": 2.5 * mm, "construction": true});
            skLineSegment(sketch, "E80.1.0.35", {"start": v(42.2, 13.87) * mm, "end": v(39.7, 15.32) * mm});
            skLineSegment(sketch, "E80.1.0.36", {"start": v(71.52, 21.58) * mm, "end": v(74.04, 20.18) * mm});
            skLineSegment(sketch, "E80.1.0.37", {"start": v(53.07, 17.25) * mm, "end": v(53.07, 20.13) * mm});
            skLineSegment(sketch, "E80.1.0.38", {"start": v(67.7, 9.54) * mm, "end": v(65.2, 10.99) * mm});
            skCircle(sketch, "E80.1.0.39", {"center": v(67.7, 12.43) * mm, "radius": 2.5 * mm, "construction": true});
            skCircle(sketch, "E80.1.0.40", {"center": v(120.57, 18.69) * mm, "radius": 2.5 * mm, "construction": true});
            skCircle(sketch, "E80.1.0.41", {"center": v(81.7, 12.43) * mm, "radius": 2.5 * mm, "construction": true});
            skLineSegment(sketch, "E80.1.0.42", {"start": v(83.07, 20.13) * mm, "end": v(85.57, 21.58) * mm});
            skLineSegment(sketch, "E80.1.0.43", {"start": v(14.2, 13.87) * mm, "end": v(11.7, 15.32) * mm});
            skLineSegment(sketch, "E80.1.0.44", {"start": v(121.2, 13.87) * mm, "end": v(123.7, 15.32) * mm});
            skLineSegment(sketch, "E80.1.0.45", {"start": v(109.07, 20.13) * mm, "end": v(109.07, 17.25) * mm});
            skCircle(sketch, "E80.1.0.46", {"center": v(99.57, 18.69) * mm, "radius": 2.5 * mm, "construction": true});
            skCircle(sketch, "E80.1.0.47", {"center": v(116.7, 12.43) * mm, "radius": 2.5 * mm, "construction": true});
            skLineSegment(sketch, "E80.1.0.48", {"start": v(114.2, 10.99) * mm, "end": v(114.2, 13.87) * mm});
            skLineSegment(sketch, "E80.1.0.49", {"start": v(53.7, 15.32) * mm, "end": v(51.2, 13.87) * mm});
            skLineSegment(sketch, "E80.1.0.50", {"start": v(105.2, 10.99) * mm, "end": v(102.7, 9.54) * mm});
            skLineSegment(sketch, "E80.1.0.51", {"start": v(41.07, 20.13) * mm, "end": v(41.07, 17.25) * mm});
            skCircle(sketch, "E80.1.0.52", {"center": v(36.57, 18.69) * mm, "radius": 2.5 * mm, "construction": true});
            skLineSegment(sketch, "E80.1.0.53", {"start": v(109.7, 15.32) * mm, "end": v(112.2, 13.87) * mm});
            skLineSegment(sketch, "E80.1.0.54", {"start": v(56.2, 10.99) * mm, "end": v(56.2, 13.87) * mm});
            skLineSegment(sketch, "E80.1.0.55", {"start": v(50.57, 21.58) * mm, "end": v(48.07, 20.13) * mm});
            skLineSegment(sketch, "E80.1.0.56", {"start": v(50.57, 15.8) * mm, "end": v(53.07, 17.25) * mm});
            skLineSegment(sketch, "E80.1.0.57", {"start": v(64.57, 21.58) * mm, "end": v(67.07, 20.13) * mm});
            skLineSegment(sketch, "E80.1.0.58", {"start": v(15.57, 21.58) * mm, "end": v(13.07, 20.13) * mm});
            skLineSegment(sketch, "E80.1.0.59", {"start": v(58.18, 11.04) * mm, "end": v(60.65, 9.54) * mm});
            skLineSegment(sketch, "E80.1.0.60", {"start": v(112.2, 10.99) * mm, "end": v(109.7, 9.54) * mm});
            skLineSegment(sketch, "E80.1.0.61", {"start": v(95.7, 15.32) * mm, "end": v(98.2, 13.87) * mm});
            skLineSegment(sketch, "E80.1.0.62", {"start": v(95.7, 9.54) * mm, "end": v(93.2, 10.99) * mm});
            skLineSegment(sketch, "E80.1.0.63", {"start": v(88.7, 9.54) * mm, "end": v(86.2, 10.99) * mm});
            skCircle(sketch, "E80.1.0.64", {"center": v(32.7, 12.43) * mm, "radius": 2.5 * mm, "construction": true});
            skLineSegment(sketch, "E80.1.0.65", {"start": v(123.7, 15.32) * mm, "end": v(126.2, 13.87) * mm});
            skLineSegment(sketch, "E80.1.0.66", {"start": v(35.2, 13.87) * mm, "end": v(32.7, 15.32) * mm});
            skCircle(sketch, "E80.1.0.67", {"center": v(109.7, 12.43) * mm, "radius": 2.5 * mm, "construction": true});
            skLineSegment(sketch, "E80.1.0.68", {"start": v(48.07, 17.25) * mm, "end": v(50.57, 15.8) * mm});
            skLineSegment(sketch, "E80.1.0.69", {"start": v(48.07, 20.13) * mm, "end": v(48.07, 17.25) * mm});
            skLineSegment(sketch, "E80.1.0.70", {"start": v(22.57, 15.8) * mm, "end": v(25.07, 17.25) * mm});
            skLineSegment(sketch, "E80.1.0.71", {"start": v(95.07, 17.25) * mm, "end": v(92.57, 15.8) * mm});
            skLineSegment(sketch, "E80.1.0.72", {"start": v(112.2, 13.87) * mm, "end": v(112.2, 10.99) * mm});
            skLineSegment(sketch, "E80.1.0.73", {"start": v(14.2, 10.99) * mm, "end": v(14.2, 13.87) * mm});
            skLineSegment(sketch, "E80.1.0.74", {"start": v(123.7, 9.54) * mm, "end": v(121.2, 10.99) * mm});
            skLineSegment(sketch, "E80.1.0.75", {"start": v(29.57, 21.58) * mm, "end": v(27.07, 20.13) * mm});
            skLineSegment(sketch, "E80.1.0.76", {"start": v(74.76, 9.54) * mm, "end": v(72.23, 10.94) * mm});
            skLineSegment(sketch, "E80.1.0.77", {"start": v(74.65, 15.32) * mm, "end": v(77.18, 13.92) * mm});
            skLineSegment(sketch, "E80.1.0.78", {"start": v(91.2, 13.87) * mm, "end": v(91.2, 10.99) * mm});
            skLineSegment(sketch, "E80.1.0.79", {"start": v(72.18, 13.82) * mm, "end": v(74.65, 15.32) * mm});
            skLineSegment(sketch, "E80.1.0.80", {"start": v(57.52, 15.8) * mm, "end": v(60.04, 17.2) * mm});
            skCircle(sketch, "E80.1.0.81", {"center": v(64.57, 18.69) * mm, "radius": 2.5 * mm, "construction": true});
            skLineSegment(sketch, "E80.1.0.82", {"start": v(43.57, 15.8) * mm, "end": v(46.07, 17.25) * mm});
            skLineSegment(sketch, "E80.1.0.83", {"start": v(90.07, 17.25) * mm, "end": v(90.07, 20.13) * mm});
            skLineSegment(sketch, "E80.1.0.84", {"start": v(13.07, 20.13) * mm, "end": v(13.07, 17.25) * mm});
            skLineSegment(sketch, "E80.1.0.85", {"start": v(69.1, 17.2) * mm, "end": v(69.04, 20.08) * mm});
            skLineSegment(sketch, "E80.1.0.86", {"start": v(78.57, 21.58) * mm, "end": v(81.07, 20.13) * mm});
            skLineSegment(sketch, "E80.1.0.87", {"start": v(6.07, 20.13) * mm, "end": v(6.07, 17.25) * mm});
            skCircle(sketch, "E80.1.0.88", {"center": v(29.57, 18.69) * mm, "radius": 2.5 * mm, "construction": true});
            skLineSegment(sketch, "E80.1.0.89", {"start": v(104.07, 20.13) * mm, "end": v(106.57, 21.58) * mm});
            skLineSegment(sketch, "E80.1.0.90", {"start": v(41.07, 17.25) * mm, "end": v(43.57, 15.8) * mm});
            skLineSegment(sketch, "E80.1.0.91", {"start": v(126.2, 13.87) * mm, "end": v(126.2, 10.99) * mm});
            skLineSegment(sketch, "E80.1.0.92", {"start": v(18.7, 15.32) * mm, "end": v(16.2, 13.87) * mm});
            skLineSegment(sketch, "E80.1.0.93", {"start": v(86.2, 13.87) * mm, "end": v(88.7, 15.32) * mm});
            skCircle(sketch, "E80.1.0.94", {"center": v(95.7, 12.43) * mm, "radius": 2.5 * mm, "construction": true});
            skLineSegment(sketch, "E80.1.0.95", {"start": v(116.7, 9.54) * mm, "end": v(114.2, 10.99) * mm});
            skCircle(sketch, "E80.1.0.96", {"center": v(74.7, 12.43) * mm, "radius": 2.5 * mm, "construction": true});
            skLineSegment(sketch, "E80.1.0.97", {"start": v(120.57, 15.8) * mm, "end": v(118.07, 17.25) * mm});
            skLineSegment(sketch, "E80.1.0.98", {"start": v(88.7, 15.32) * mm, "end": v(91.2, 13.87) * mm});
            skLineSegment(sketch, "E80.1.0.99", {"start": v(11.07, 17.25) * mm, "end": v(11.07, 20.13) * mm});
            skCircle(sketch, "E80.1.0.100", {"center": v(102.7, 12.43) * mm, "radius": 2.5 * mm, "construction": true});
            skLineSegment(sketch, "E80.1.0.101", {"start": v(97.07, 20.13) * mm, "end": v(99.57, 21.58) * mm});
            skLineSegment(sketch, "E80.1.0.102", {"start": v(39.07, 17.25) * mm, "end": v(39.07, 20.13) * mm});
            skLineSegment(sketch, "E80.1.0.103", {"start": v(25.07, 17.25) * mm, "end": v(25.07, 20.13) * mm});
            skLineSegment(sketch, "E80.1.0.104", {"start": v(74.04, 20.18) * mm, "end": v(74.1, 17.3) * mm});
            skCircle(sketch, "E80.1.0.105", {"center": v(11.7, 12.43) * mm, "radius": 2.5 * mm, "construction": true});
            skLineSegment(sketch, "E80.1.0.106", {"start": v(107.2, 13.87) * mm, "end": v(109.7, 15.32) * mm});
            skLineSegment(sketch, "E80.1.0.107", {"start": v(36.57, 15.8) * mm, "end": v(39.07, 17.25) * mm});
            skLineSegment(sketch, "E80.1.0.108", {"start": v(25.7, 15.32) * mm, "end": v(23.2, 13.87) * mm});
            skLineSegment(sketch, "E80.1.0.109", {"start": v(11.7, 15.32) * mm, "end": v(9.2, 13.87) * mm});
            skLineSegment(sketch, "E80.1.0.110", {"start": v(63.23, 13.82) * mm, "end": v(60.76, 15.32) * mm});
            skLineSegment(sketch, "E80.1.0.111", {"start": v(105.2, 13.87) * mm, "end": v(105.2, 10.99) * mm});
            skLineSegment(sketch, "E80.1.0.112", {"start": v(116.7, 15.32) * mm, "end": v(119.2, 13.87) * mm});
            skLineSegment(sketch, "E80.1.0.113", {"start": v(98.2, 13.87) * mm, "end": v(98.2, 10.99) * mm});
            skLineSegment(sketch, "E80.1.0.114", {"start": v(32.07, 20.13) * mm, "end": v(29.57, 21.58) * mm});
            skCircle(sketch, "E80.1.0.115", {"center": v(50.57, 18.69) * mm, "radius": 2.5 * mm, "construction": true});
            skLineSegment(sketch, "E80.1.0.116", {"start": v(46.07, 20.13) * mm, "end": v(43.57, 21.58) * mm});
            skLineSegment(sketch, "E80.1.0.117", {"start": v(102.07, 17.25) * mm, "end": v(99.57, 15.8) * mm});
            skLineSegment(sketch, "E80.1.0.118", {"start": v(106.57, 15.8) * mm, "end": v(104.07, 17.25) * mm});
            skLineSegment(sketch, "E80.1.0.119", {"start": v(113.57, 15.8) * mm, "end": v(111.07, 17.25) * mm});
            skLineSegment(sketch, "E80.1.0.120", {"start": v(71.63, 15.8) * mm, "end": v(69.1, 17.2) * mm});
            skLineSegment(sketch, "E80.1.0.121", {"start": v(116.07, 17.25) * mm, "end": v(113.57, 15.8) * mm});
            skLineSegment(sketch, "E80.1.0.122", {"start": v(104.07, 17.25) * mm, "end": v(104.07, 20.13) * mm});
            skLineSegment(sketch, "E80.1.0.123", {"start": v(11.7, 9.54) * mm, "end": v(14.2, 10.99) * mm});
            skCircle(sketch, "E80.1.0.124", {"center": v(53.7, 12.43) * mm, "radius": 2.5 * mm, "construction": true});
            skLineSegment(sketch, "E80.1.0.125", {"start": v(93.2, 13.87) * mm, "end": v(95.7, 15.32) * mm});
            skLineSegment(sketch, "E80.1.0.126", {"start": v(62.07, 17.25) * mm, "end": v(62.07, 20.13) * mm});
            skLineSegment(sketch, "E80.1.0.127", {"start": v(25.07, 20.13) * mm, "end": v(22.57, 21.58) * mm});
            skLineSegment(sketch, "E80.1.0.128", {"start": v(67.07, 20.13) * mm, "end": v(67.07, 17.25) * mm});
            skLineSegment(sketch, "E80.1.0.129", {"start": v(64.57, 15.8) * mm, "end": v(62.07, 17.25) * mm});
            skCircle(sketch, "E80.1.0.130", {"center": v(22.57, 18.69) * mm, "radius": 2.5 * mm, "construction": true});
            skLineSegment(sketch, "E80.1.0.131", {"start": v(120.57, 21.58) * mm, "end": v(123.07, 20.13) * mm});
            skCircle(sketch, "E80.1.0.132", {"center": v(60.7, 12.43) * mm, "radius": 2.5 * mm, "construction": true});
            skLineSegment(sketch, "E80.1.0.133", {"start": v(111.07, 17.25) * mm, "end": v(111.07, 20.13) * mm});
            skCircle(sketch, "E80.1.0.134", {"center": v(71.57, 18.69) * mm, "radius": 2.5 * mm, "construction": true});
            skLineSegment(sketch, "E80.1.0.135", {"start": v(6.07, 17.25) * mm, "end": v(8.57, 15.8) * mm});
            skLineSegment(sketch, "E80.1.0.136", {"start": v(85.57, 21.58) * mm, "end": v(88.07, 20.13) * mm});
            skLineSegment(sketch, "E80.1.0.137", {"start": v(100.2, 10.99) * mm, "end": v(100.2, 13.87) * mm});
            skLineSegment(sketch, "E80.1.0.138", {"start": v(53.7, 9.54) * mm, "end": v(56.2, 10.99) * mm});
            skLineSegment(sketch, "E80.1.0.139", {"start": v(39.07, 20.13) * mm, "end": v(36.57, 21.58) * mm});
            skLineSegment(sketch, "E80.1.0.140", {"start": v(81.07, 17.25) * mm, "end": v(78.57, 15.8) * mm});
            skLineSegment(sketch, "E80.1.0.141", {"start": v(99.57, 15.8) * mm, "end": v(97.07, 17.25) * mm});
            skLineSegment(sketch, "E80.1.0.142", {"start": v(83.07, 17.25) * mm, "end": v(83.07, 20.13) * mm});
            skLineSegment(sketch, "E80.1.0.143", {"start": v(20.07, 17.25) * mm, "end": v(22.57, 15.8) * mm});
            skCircle(sketch, "E80.1.0.144", {"center": v(15.57, 18.69) * mm, "radius": 2.5 * mm, "construction": true});
            skLineSegment(sketch, "E80.1.0.145", {"start": v(67.7, 15.32) * mm, "end": v(70.2, 13.87) * mm});
            skLineSegment(sketch, "E80.1.0.146", {"start": v(116.07, 20.13) * mm, "end": v(116.07, 17.25) * mm});
            skLineSegment(sketch, "E80.1.0.147", {"start": v(18.07, 20.13) * mm, "end": v(15.57, 21.58) * mm});
            skCircle(sketch, "E80.1.0.148", {"center": v(8.57, 18.69) * mm, "radius": 2.5 * mm, "construction": true});
            skLineSegment(sketch, "E80.1.0.149", {"start": v(118.07, 17.25) * mm, "end": v(118.07, 20.13) * mm});
            skCircle(sketch, "E80.1.0.150", {"center": v(92.57, 18.69) * mm, "radius": 2.5 * mm, "construction": true});
            skLineSegment(sketch, "E80.1.0.151", {"start": v(55.04, 17.3) * mm, "end": v(57.52, 15.8) * mm});
            skLineSegment(sketch, "E80.1.0.152", {"start": v(86.2, 10.99) * mm, "end": v(86.2, 13.87) * mm});
            skLineSegment(sketch, "E80.1.0.153", {"start": v(42.2, 10.99) * mm, "end": v(42.2, 13.87) * mm});
            skLineSegment(sketch, "E80.1.0.154", {"start": v(77.23, 11.04) * mm, "end": v(74.76, 9.54) * mm});
            skLineSegment(sketch, "E80.1.0.155", {"start": v(46.7, 9.54) * mm, "end": v(49.2, 10.99) * mm});
            skCircle(sketch, "E80.1.0.156", {"center": v(25.7, 12.43) * mm, "radius": 2.5 * mm, "construction": true});
            skLineSegment(sketch, "E80.1.0.157", {"start": v(77.18, 13.92) * mm, "end": v(77.23, 11.04) * mm});
            skLineSegment(sketch, "E80.1.0.158", {"start": v(36.57, 21.58) * mm, "end": v(34.07, 20.13) * mm});
            skLineSegment(sketch, "E80.1.0.159", {"start": v(99.57, 21.58) * mm, "end": v(102.07, 20.13) * mm});
            skCircle(sketch, "E80.1.0.160", {"center": v(85.57, 18.69) * mm, "radius": 2.5 * mm, "construction": true});
            skLineSegment(sketch, "E80.1.0.161", {"start": v(13.07, 17.25) * mm, "end": v(15.57, 15.8) * mm});
            skCircle(sketch, "E80.1.0.162", {"center": v(106.57, 18.69) * mm, "radius": 2.5 * mm, "construction": true});
            skLineSegment(sketch, "E80.1.0.163", {"start": v(97.07, 17.25) * mm, "end": v(97.07, 20.13) * mm});
            skLineSegment(sketch, "E80.1.0.164", {"start": v(102.7, 9.54) * mm, "end": v(100.2, 10.99) * mm});
            skLineSegment(sketch, "E80.1.0.165", {"start": v(37.2, 13.87) * mm, "end": v(37.2, 10.99) * mm});
            skCircle(sketch, "E80.1.0.166", {"center": v(123.7, 12.43) * mm, "radius": 2.5 * mm, "construction": true});
            skLineSegment(sketch, "E80.1.0.167", {"start": v(114.2, 13.87) * mm, "end": v(116.7, 15.32) * mm});
            skLineSegment(sketch, "E80.1.0.168", {"start": v(81.07, 20.13) * mm, "end": v(81.07, 17.25) * mm});
            skLineSegment(sketch, "E80.1.0.169", {"start": v(93.2, 10.99) * mm, "end": v(93.2, 13.87) * mm});
            skLineSegment(sketch, "E80.1.0.170", {"start": v(84.2, 10.99) * mm, "end": v(81.7, 9.54) * mm});
            skLineSegment(sketch, "E80.1.0.171", {"start": v(39.7, 9.54) * mm, "end": v(42.2, 10.99) * mm});
            skLineSegment(sketch, "E80.1.0.172", {"start": v(23.2, 10.99) * mm, "end": v(25.7, 9.54) * mm});
            skCircle(sketch, "E80.1.0.173", {"center": v(57.57, 18.69) * mm, "radius": 2.5 * mm, "construction": true});
            skLineSegment(sketch, "E80.1.0.174", {"start": v(35.2, 10.99) * mm, "end": v(35.2, 13.87) * mm});
            skLineSegment(sketch, "E80.1.0.175", {"start": v(92.57, 21.58) * mm, "end": v(95.07, 20.13) * mm});
            skLineSegment(sketch, "E80.1.0.176", {"start": v(32.7, 9.54) * mm, "end": v(35.2, 10.99) * mm});
            skLineSegment(sketch, "E80.1.0.177", {"start": v(65.2, 13.87) * mm, "end": v(67.7, 15.32) * mm});
            skLineSegment(sketch, "E80.1.0.178", {"start": v(60.65, 9.54) * mm, "end": v(63.18, 10.94) * mm});
            skLineSegment(sketch, "E80.1.0.179", {"start": v(74.1, 17.3) * mm, "end": v(71.63, 15.8) * mm});
            skLineSegment(sketch, "E80.1.0.180", {"start": v(16.2, 13.87) * mm, "end": v(16.2, 10.99) * mm});
            skLineSegment(sketch, "E80.1.0.181", {"start": v(118.07, 20.13) * mm, "end": v(120.57, 21.58) * mm});
            skLineSegment(sketch, "E80.1.0.182", {"start": v(60.1, 20.08) * mm, "end": v(57.63, 21.58) * mm});
            skLineSegment(sketch, "E80.1.0.183", {"start": v(88.07, 17.25) * mm, "end": v(85.57, 15.8) * mm});
            skCircle(sketch, "E80.1.0.184", {"center": v(88.7, 12.43) * mm, "radius": 2.5 * mm, "construction": true});
            skLineSegment(sketch, "E80.1.0.185", {"start": v(27.07, 17.25) * mm, "end": v(29.57, 15.8) * mm});
            skLineSegment(sketch, "E80.1.0.186", {"start": v(51.2, 13.87) * mm, "end": v(51.2, 10.99) * mm});
            skLineSegment(sketch, "E80.1.0.187", {"start": v(43.57, 21.58) * mm, "end": v(41.07, 20.13) * mm});
            skLineSegment(sketch, "E80.1.0.188", {"start": v(102.7, 15.32) * mm, "end": v(105.2, 13.87) * mm});
            skLineSegment(sketch, "E80.1.0.189", {"start": v(55.1, 20.18) * mm, "end": v(55.04, 17.3) * mm});
            skLineSegment(sketch, "E80.1.0.190", {"start": v(65.2, 10.99) * mm, "end": v(65.2, 13.87) * mm});
            skLineSegment(sketch, "E80.1.0.191", {"start": v(90.07, 20.13) * mm, "end": v(92.57, 21.58) * mm});
            skLineSegment(sketch, "E80.1.0.192", {"start": v(92.57, 15.8) * mm, "end": v(90.07, 17.25) * mm});
            skLineSegment(sketch, "E80.1.0.193", {"start": v(70.2, 10.99) * mm, "end": v(67.7, 9.54) * mm});
            skLineSegment(sketch, "E80.1.0.194", {"start": v(8.57, 15.8) * mm, "end": v(11.07, 17.25) * mm});
            skLineSegment(sketch, "E80.1.0.195", {"start": v(28.2, 13.87) * mm, "end": v(25.7, 15.32) * mm});
            skCircle(sketch, "E80.1.0.196", {"center": v(78.57, 18.69) * mm, "radius": 2.5 * mm, "construction": true});
            skLineSegment(sketch, "E80.1.0.197", {"start": v(15.57, 15.8) * mm, "end": v(18.07, 17.25) * mm});
            skLineSegment(sketch, "E80.1.0.198", {"start": v(106.57, 21.58) * mm, "end": v(109.07, 20.13) * mm});
            skCircle(sketch, "E80.1.0.199", {"center": v(113.57, 18.69) * mm, "radius": 2.5 * mm, "construction": true});
            skLineSegment(sketch, "E80.1.0.200", {"start": v(67.07, 17.25) * mm, "end": v(64.57, 15.8) * mm});
            skLineSegment(sketch, "E80.1.0.201", {"start": v(102.07, 20.13) * mm, "end": v(102.07, 17.25) * mm});
            skLineSegment(sketch, "E80.1.0.202", {"start": v(34.07, 17.25) * mm, "end": v(36.57, 15.8) * mm});
            skLineSegment(sketch, "E80.1.0.203", {"start": v(95.07, 20.13) * mm, "end": v(95.07, 17.25) * mm});
            skLineSegment(sketch, "E80.1.0.204", {"start": v(57.63, 21.58) * mm, "end": v(55.1, 20.18) * mm});
            skLineSegment(sketch, "E80.1.0.205", {"start": v(109.07, 17.25) * mm, "end": v(106.57, 15.8) * mm});
            skLineSegment(sketch, "E80.1.0.206", {"start": v(76.07, 17.25) * mm, "end": v(76.07, 20.13) * mm});
            skLineSegment(sketch, "E80.1.0.207", {"start": v(107.2, 10.99) * mm, "end": v(107.2, 13.87) * mm});
            skLineSegment(sketch, "E80.1.0.208", {"start": v(98.2, 10.99) * mm, "end": v(95.7, 9.54) * mm});
            skLineSegment(sketch, "E80.1.0.209", {"start": v(81.7, 15.32) * mm, "end": v(84.2, 13.87) * mm});
            skLineSegment(sketch, "E80.1.0.210", {"start": v(60.76, 15.32) * mm, "end": v(58.23, 13.92) * mm});
            skLineSegment(sketch, "E80.1.0.211", {"start": v(21.2, 13.87) * mm, "end": v(18.7, 15.32) * mm});
            skLineSegment(sketch, "E80.1.0.212", {"start": v(30.2, 10.99) * mm, "end": v(32.7, 9.54) * mm});
            skLineSegment(sketch, "E80.1.0.213", {"start": v(53.07, 20.13) * mm, "end": v(50.57, 21.58) * mm});
            skLineSegment(sketch, "E80.1.0.214", {"start": v(76.07, 20.13) * mm, "end": v(78.57, 21.58) * mm});
            skLineSegment(sketch, "E80.1.0.215", {"start": v(111.07, 20.13) * mm, "end": v(113.57, 21.58) * mm});
            skLineSegment(sketch, "E80.1.0.216", {"start": v(72.23, 10.94) * mm, "end": v(72.18, 13.82) * mm});
            skLineSegment(sketch, "E80.1.0.217", {"start": v(39.7, 15.32) * mm, "end": v(37.2, 13.87) * mm});
            skLineSegment(sketch, "E80.1.0.218", {"start": v(78.57, 15.8) * mm, "end": v(76.07, 17.25) * mm});
            skLineSegment(sketch, "E80.1.0.219", {"start": v(60.04, 17.2) * mm, "end": v(60.1, 20.08) * mm});
            skLineSegment(sketch, "E80.1.0.220", {"start": v(88.07, 20.13) * mm, "end": v(88.07, 17.25) * mm});
            skLineSegment(sketch, "E80.1.0.221", {"start": v(18.07, 17.25) * mm, "end": v(18.07, 20.13) * mm});
            skLineSegment(sketch, "E80.1.0.222", {"start": v(100.2, 13.87) * mm, "end": v(102.7, 15.32) * mm});
            skLineSegment(sketch, "E80.1.0.223", {"start": v(62.07, 20.13) * mm, "end": v(64.57, 21.58) * mm});
            skLineSegment(sketch, "E80.1.0.224", {"start": v(9.2, 10.99) * mm, "end": v(11.7, 9.54) * mm});
            skLineSegment(sketch, "E80.1.0.225", {"start": v(46.07, 17.25) * mm, "end": v(46.07, 20.13) * mm});
            skLineSegment(sketch, "E80.1.0.226", {"start": v(109.7, 9.54) * mm, "end": v(107.2, 10.99) * mm});
            skLineSegment(sketch, "E80.1.0.227", {"start": v(84.2, 13.87) * mm, "end": v(84.2, 10.99) * mm});
            skLineSegment(sketch, "E80.1.0.228", {"start": v(8.57, 21.58) * mm, "end": v(6.07, 20.13) * mm});
            skLineSegment(sketch, "E80.1.0.229", {"start": v(11.07, 20.13) * mm, "end": v(8.57, 21.58) * mm});
            skLineSegment(sketch, "E80.1.0.230", {"start": v(113.57, 21.58) * mm, "end": v(116.07, 20.13) * mm});
            skLineSegment(sketch, "E80.1.0.231", {"start": v(18.7, 9.54) * mm, "end": v(21.2, 10.99) * mm});
            skLineSegment(sketch, "E80.1.0.232", {"start": v(28.2, 10.99) * mm, "end": v(28.2, 13.87) * mm});
            skLineSegment(sketch, "E80.1.0.233", {"start": v(63.18, 10.94) * mm, "end": v(63.23, 13.82) * mm});
            skLineSegment(sketch, "E80.1.0.234", {"start": v(69.04, 20.08) * mm, "end": v(71.52, 21.58) * mm});
            skLineSegment(sketch, "E80.1.0.235", {"start": v(34.07, 20.13) * mm, "end": v(34.07, 17.25) * mm});
            skLineSegment(sketch, "E80.1.0.236", {"start": v(70.2, 13.87) * mm, "end": v(70.2, 10.99) * mm});
            skLineSegment(sketch, "E80.1.0.237", {"start": v(32.7, 15.32) * mm, "end": v(30.2, 13.87) * mm});
            skLineSegment(sketch, "E80.1.0.238", {"start": v(49.2, 10.99) * mm, "end": v(49.2, 13.87) * mm});
            skLineSegment(sketch, "E80.2.0.1", {"start": v(126.53, 23.42) * mm, "end": v(124.03, 21.97) * mm});
            skLineSegment(sketch, "E80.2.0.3", {"start": v(119.53, 23.42) * mm, "end": v(117.03, 21.97) * mm});
            skLineSegment(sketch, "E80.2.0.7", {"start": v(51.53, 23.42) * mm, "end": v(54.03, 21.97) * mm});
            skLineSegment(sketch, "E80.2.0.8", {"start": v(91.53, 23.42) * mm, "end": v(89.03, 21.97) * mm});
            skLineSegment(sketch, "E80.2.0.13", {"start": v(26.03, 21.97) * mm, "end": v(28.53, 23.42) * mm});
            skLineSegment(sketch, "E80.2.0.17", {"start": v(37.53, 23.42) * mm, "end": v(40.03, 21.97) * mm});
            skLineSegment(sketch, "E80.2.0.21", {"start": v(44.53, 23.42) * mm, "end": v(47.03, 21.97) * mm});
            skLineSegment(sketch, "E80.2.0.26", {"start": v(16.53, 23.42) * mm, "end": v(19.03, 21.97) * mm});
            skLineSegment(sketch, "E80.2.0.29", {"start": v(82.03, 21.97) * mm, "end": v(79.53, 23.42) * mm});
            skLineSegment(sketch, "E80.2.0.38", {"start": v(68.03, 21.97) * mm, "end": v(65.53, 23.42) * mm});
            skLineSegment(sketch, "E80.2.0.50", {"start": v(105.53, 23.42) * mm, "end": v(103.03, 21.97) * mm});
            skLineSegment(sketch, "E80.2.0.59", {"start": v(58.5, 23.47) * mm, "end": v(60.98, 21.97) * mm});
            skLineSegment(sketch, "E80.2.0.60", {"start": v(112.53, 23.42) * mm, "end": v(110.03, 21.97) * mm});
            skLineSegment(sketch, "E80.2.0.62", {"start": v(96.03, 21.97) * mm, "end": v(93.53, 23.42) * mm});
            skLineSegment(sketch, "E80.2.0.63", {"start": v(89.03, 21.97) * mm, "end": v(86.53, 23.42) * mm});
            skLineSegment(sketch, "E80.2.0.74", {"start": v(124.03, 21.97) * mm, "end": v(121.53, 23.42) * mm});
            skLineSegment(sketch, "E80.2.0.76", {"start": v(75.1, 21.97) * mm, "end": v(72.56, 23.37) * mm});
            skLineSegment(sketch, "E80.2.0.95", {"start": v(117.03, 21.97) * mm, "end": v(114.53, 23.42) * mm});
            skLineSegment(sketch, "E80.2.0.123", {"start": v(12.03, 21.97) * mm, "end": v(14.53, 23.42) * mm});
            skLineSegment(sketch, "E80.2.0.138", {"start": v(54.03, 21.97) * mm, "end": v(56.53, 23.42) * mm});
            skLineSegment(sketch, "E80.2.0.154", {"start": v(77.56, 23.47) * mm, "end": v(75.1, 21.97) * mm});
            skLineSegment(sketch, "E80.2.0.155", {"start": v(47.03, 21.97) * mm, "end": v(49.53, 23.42) * mm});
            skLineSegment(sketch, "E80.2.0.164", {"start": v(103.03, 21.97) * mm, "end": v(100.53, 23.42) * mm});
            skLineSegment(sketch, "E80.2.0.170", {"start": v(84.53, 23.42) * mm, "end": v(82.03, 21.97) * mm});
            skLineSegment(sketch, "E80.2.0.171", {"start": v(40.03, 21.97) * mm, "end": v(42.53, 23.42) * mm});
            skLineSegment(sketch, "E80.2.0.172", {"start": v(23.53, 23.42) * mm, "end": v(26.03, 21.97) * mm});
            skLineSegment(sketch, "E80.2.0.176", {"start": v(33.03, 21.97) * mm, "end": v(35.53, 23.42) * mm});
            skLineSegment(sketch, "E80.2.0.178", {"start": v(60.98, 21.97) * mm, "end": v(63.5, 23.37) * mm});
            skLineSegment(sketch, "E80.2.0.193", {"start": v(70.53, 23.42) * mm, "end": v(68.03, 21.97) * mm});
            skLineSegment(sketch, "E80.2.0.208", {"start": v(98.53, 23.42) * mm, "end": v(96.03, 21.97) * mm});
            skLineSegment(sketch, "E80.2.0.212", {"start": v(30.53, 23.42) * mm, "end": v(33.03, 21.97) * mm});
            skLineSegment(sketch, "E80.2.0.224", {"start": v(9.53, 23.42) * mm, "end": v(12.03, 21.97) * mm});
            skLineSegment(sketch, "E80.2.0.226", {"start": v(110.03, 21.97) * mm, "end": v(107.53, 23.42) * mm});
            skLineSegment(sketch, "E80.2.0.231", {"start": v(19.03, 21.97) * mm, "end": v(21.53, 23.42) * mm});
            skLineSegment(sketch, "E80.direction1", {"start": v(8.88, -1.44) * mm, "end": v(9.2, 10.99) * mm, "construction": true});
            skLineSegment(sketch, "E81.1.0.0", {"start": v(24.47, -4.73) * mm, "end": v(21.97, -3.28) * mm});
            skLineSegment(sketch, "E81.1.0.1", {"start": v(75.47, -4.73) * mm, "end": v(77.97, -3.28) * mm});
            skLineSegment(sketch, "E81.1.0.2", {"start": v(54.44, -7.57) * mm, "end": v(56.91, -9.06) * mm});
            skLineSegment(sketch, "E81.1.0.3", {"start": v(48.6, -13.87) * mm, "end": v(48.6, -10.99) * mm});
            skLineSegment(sketch, "E81.1.0.4", {"start": v(20.6, -10.99) * mm, "end": v(18.1, -9.54) * mm});
            skCircle(sketch, "E81.1.0.5", {"center": v(35.97, -6.17) * mm, "radius": 2.5 * mm, "construction": true});
            skLineSegment(sketch, "E81.1.0.6", {"start": v(53.1, -15.32) * mm, "end": v(55.6, -13.87) * mm});
            skCircle(sketch, "E81.1.0.7", {"center": v(63.97, -6.17) * mm, "radius": 2.5 * mm, "construction": true});
            skLineSegment(sketch, "E81.1.0.8", {"start": v(20.6, -13.87) * mm, "end": v(20.6, -10.99) * mm});
            skCircle(sketch, "E81.1.0.9", {"center": v(28.97, -6.17) * mm, "radius": 2.5 * mm, "construction": true});
            skCircle(sketch, "E81.1.0.10", {"center": v(70.97, -6.17) * mm, "radius": 2.5 * mm, "construction": true});
            skLineSegment(sketch, "E81.1.0.11", {"start": v(110.47, -7.61) * mm, "end": v(110.47, -4.73) * mm});
            skLineSegment(sketch, "E81.1.0.12", {"start": v(61.47, -7.61) * mm, "end": v(61.47, -4.73) * mm});
            skLineSegment(sketch, "E81.1.0.13", {"start": v(94.47, -4.73) * mm, "end": v(94.47, -7.61) * mm});
            skLineSegment(sketch, "E81.1.0.14", {"start": v(5.47, -4.73) * mm, "end": v(5.47, -7.61) * mm});
            skLineSegment(sketch, "E81.1.0.15", {"start": v(8.6, -13.87) * mm, "end": v(5.47, -7.61) * mm, "construction": true});
            skLineSegment(sketch, "E81.1.0.16", {"start": v(56.91, -9.06) * mm, "end": v(59.44, -7.66) * mm});
            skCircle(sketch, "E81.1.0.17", {"center": v(11.1, -12.43) * mm, "radius": 2.5 * mm, "construction": true});
            skLineSegment(sketch, "E81.1.0.18", {"start": v(40.47, -7.61) * mm, "end": v(42.97, -9.06) * mm});
            skLineSegment(sketch, "E81.1.0.19", {"start": v(103.47, -4.73) * mm, "end": v(105.97, -3.28) * mm});
            skCircle(sketch, "E81.1.0.20", {"center": v(14.97, -6.17) * mm, "radius": 2.5 * mm, "construction": true});
            skLineSegment(sketch, "E81.1.0.21", {"start": v(76.63, -13.83) * mm, "end": v(74.16, -15.32) * mm});
            skLineSegment(sketch, "E81.1.0.22", {"start": v(102.1, -15.32) * mm, "end": v(99.6, -13.87) * mm});
            skCircle(sketch, "E81.1.0.23", {"center": v(109.1, -12.43) * mm, "radius": 2.5 * mm, "construction": true});
            skLineSegment(sketch, "E81.1.0.24", {"start": v(73.44, -4.68) * mm, "end": v(73.5, -7.57) * mm});
            skLineSegment(sketch, "E81.1.0.25", {"start": v(46.1, -15.32) * mm, "end": v(48.6, -13.87) * mm});
            skCircle(sketch, "E81.1.0.26", {"center": v(84.97, -6.17) * mm, "radius": 2.5 * mm, "construction": true});
            skLineSegment(sketch, "E81.1.0.27", {"start": v(21.97, -3.28) * mm, "end": v(19.47, -4.73) * mm});
            skCircle(sketch, "E81.1.0.28", {"center": v(105.97, -6.17) * mm, "radius": 2.5 * mm, "construction": true});
            skLineSegment(sketch, "E81.1.0.29", {"start": v(42.97, -9.06) * mm, "end": v(45.47, -7.61) * mm});
            skLineSegment(sketch, "E81.1.0.30", {"start": v(36.6, -10.99) * mm, "end": v(36.6, -13.87) * mm});
            skCircle(sketch, "E81.1.0.31", {"center": v(74.1, -12.43) * mm, "radius": 2.5 * mm, "construction": true});
            skLineSegment(sketch, "E81.1.0.32", {"start": v(64.6, -10.99) * mm, "end": v(67.1, -9.54) * mm});
            skLineSegment(sketch, "E81.1.0.33", {"start": v(64.6, -13.87) * mm, "end": v(64.6, -10.99) * mm});
            skCircle(sketch, "E81.1.0.34", {"center": v(91.97, -6.17) * mm, "radius": 2.5 * mm, "construction": true});
            skCircle(sketch, "E81.1.0.35", {"center": v(56.97, -6.17) * mm, "radius": 2.5 * mm, "construction": true});
            skCircle(sketch, "E81.1.0.36", {"center": v(25.1, -12.43) * mm, "radius": 2.5 * mm, "construction": true});
            skLineSegment(sketch, "E81.1.0.37", {"start": v(15.6, -10.99) * mm, "end": v(15.6, -13.87) * mm});
            skLineSegment(sketch, "E81.1.0.38", {"start": v(34.6, -13.87) * mm, "end": v(34.6, -10.99) * mm});
            skLineSegment(sketch, "E81.1.0.39", {"start": v(60.05, -15.32) * mm, "end": v(62.57, -13.92) * mm});
            skCircle(sketch, "E81.1.0.40", {"center": v(88.1, -12.43) * mm, "radius": 2.5 * mm, "construction": true});
            skLineSegment(sketch, "E81.1.0.41", {"start": v(11.1, -9.54) * mm, "end": v(8.6, -10.99) * mm});
            skCircle(sketch, "E81.1.0.42", {"center": v(46.1, -12.43) * mm, "radius": 2.5 * mm, "construction": true});
            skLineSegment(sketch, "E81.1.0.43", {"start": v(99.6, -13.87) * mm, "end": v(99.6, -10.99) * mm});
            skLineSegment(sketch, "E81.1.0.44", {"start": v(49.97, -3.28) * mm, "end": v(47.47, -4.73) * mm});
            skLineSegment(sketch, "E81.1.0.45", {"start": v(115.47, -7.61) * mm, "end": v(112.97, -9.06) * mm});
            skLineSegment(sketch, "E81.1.0.46", {"start": v(19.47, -7.61) * mm, "end": v(21.97, -9.06) * mm});
            skLineSegment(sketch, "E81.1.0.47", {"start": v(119.97, -3.28) * mm, "end": v(122.47, -4.73) * mm});
            skLineSegment(sketch, "E81.1.0.48", {"start": v(21.97, -9.06) * mm, "end": v(24.47, -7.61) * mm});
            skLineSegment(sketch, "E81.1.0.49", {"start": v(122.47, -4.73) * mm, "end": v(122.47, -7.61) * mm});
            skLineSegment(sketch, "E81.1.0.50", {"start": v(29.6, -13.87) * mm, "end": v(32.1, -15.32) * mm});
            skCircle(sketch, "E81.1.0.51", {"center": v(18.1, -12.43) * mm, "radius": 2.5 * mm, "construction": true});
            skLineSegment(sketch, "E81.1.0.52", {"start": v(57.63, -10.94) * mm, "end": v(57.57, -13.83) * mm});
            skCircle(sketch, "E81.1.0.53", {"center": v(81.1, -12.43) * mm, "radius": 2.5 * mm, "construction": true});
            skCircle(sketch, "E81.1.0.54", {"center": v(21.97, -6.17) * mm, "radius": 2.5 * mm, "construction": true});
            skLineSegment(sketch, "E81.1.0.55", {"start": v(55.6, -13.87) * mm, "end": v(55.6, -10.99) * mm});
            skLineSegment(sketch, "E81.1.0.56", {"start": v(27.6, -10.99) * mm, "end": v(25.1, -9.54) * mm});
            skCircle(sketch, "E81.1.0.57", {"center": v(123.1, -12.43) * mm, "radius": 2.5 * mm, "construction": true});
            skCircle(sketch, "E81.1.0.58", {"center": v(7.97, -6.17) * mm, "radius": 2.5 * mm, "construction": true});
            skLineSegment(sketch, "E81.1.0.59", {"start": v(22.6, -10.99) * mm, "end": v(22.6, -13.87) * mm});
            skLineSegment(sketch, "E81.1.0.60", {"start": v(57.03, -3.29) * mm, "end": v(54.5, -4.68) * mm});
            skLineSegment(sketch, "E81.1.0.61", {"start": v(26.47, -4.73) * mm, "end": v(26.47, -7.61) * mm});
            skLineSegment(sketch, "E81.1.0.62", {"start": v(75.47, -7.61) * mm, "end": v(75.47, -4.73) * mm});
            skLineSegment(sketch, "E81.1.0.63", {"start": v(38.47, -7.61) * mm, "end": v(38.47, -4.73) * mm});
            skLineSegment(sketch, "E81.1.0.64", {"start": v(116.1, -9.54) * mm, "end": v(118.6, -10.99) * mm});
            skLineSegment(sketch, "E81.1.0.65", {"start": v(125.6, -10.99) * mm, "end": v(125.6, -13.87) * mm});
            skCircle(sketch, "E81.1.0.66", {"center": v(49.97, -6.17) * mm, "radius": 2.5 * mm, "construction": true});
            skCircle(sketch, "E81.1.0.67", {"center": v(102.1, -12.43) * mm, "radius": 2.5 * mm, "construction": true});
            skCircle(sketch, "E81.1.0.68", {"center": v(67.1, -12.43) * mm, "radius": 2.5 * mm, "construction": true});
            skLineSegment(sketch, "E81.1.0.69", {"start": v(69.6, -10.99) * mm, "end": v(69.6, -13.87) * mm});
            skLineSegment(sketch, "E81.1.0.70", {"start": v(25.1, -15.32) * mm, "end": v(27.6, -13.87) * mm});
            skLineSegment(sketch, "E81.1.0.71", {"start": v(69.6, -13.87) * mm, "end": v(67.1, -15.32) * mm});
            skCircle(sketch, "E81.1.0.72", {"center": v(32.1, -12.43) * mm, "radius": 2.5 * mm, "construction": true});
            skLineSegment(sketch, "E81.1.0.73", {"start": v(120.6, -13.87) * mm, "end": v(120.6, -10.99) * mm});
            skCircle(sketch, "E81.1.0.74", {"center": v(39.1, -12.43) * mm, "radius": 2.5 * mm, "construction": true});
            skLineSegment(sketch, "E81.1.0.75", {"start": v(118.6, -13.87) * mm, "end": v(116.1, -15.32) * mm});
            skLineSegment(sketch, "E81.1.0.76", {"start": v(111.6, -13.87) * mm, "end": v(109.1, -15.32) * mm});
            skLineSegment(sketch, "E81.1.0.77", {"start": v(71.63, -13.92) * mm, "end": v(71.57, -11.04) * mm});
            skLineSegment(sketch, "E81.1.0.78", {"start": v(18.1, -9.54) * mm, "end": v(15.6, -10.99) * mm});
            skLineSegment(sketch, "E81.1.0.79", {"start": v(41.6, -10.99) * mm, "end": v(39.1, -9.54) * mm});
            skLineSegment(sketch, "E81.1.0.80", {"start": v(46.1, -9.54) * mm, "end": v(43.6, -10.99) * mm});
            skLineSegment(sketch, "E81.1.0.81", {"start": v(63.97, -3.28) * mm, "end": v(66.47, -4.73) * mm});
            skLineSegment(sketch, "E81.1.0.82", {"start": v(49.97, -9.06) * mm, "end": v(52.47, -7.61) * mm});
            skLineSegment(sketch, "E81.1.0.83", {"start": v(17.47, -7.61) * mm, "end": v(17.47, -4.73) * mm});
            skLineSegment(sketch, "E81.1.0.84", {"start": v(97.6, -13.87) * mm, "end": v(95.1, -15.32) * mm});
            skLineSegment(sketch, "E81.1.0.85", {"start": v(25.1, -9.54) * mm, "end": v(22.6, -10.99) * mm});
            skLineSegment(sketch, "E81.1.0.86", {"start": v(33.47, -7.61) * mm, "end": v(35.97, -9.06) * mm});
            skCircle(sketch, "E81.1.0.87", {"center": v(95.1, -12.43) * mm, "radius": 2.5 * mm, "construction": true});
            skLineSegment(sketch, "E81.1.0.88", {"start": v(101.47, -4.73) * mm, "end": v(101.47, -7.61) * mm});
            skLineSegment(sketch, "E81.1.0.89", {"start": v(70.91, -3.29) * mm, "end": v(73.44, -4.68) * mm});
            skLineSegment(sketch, "E81.1.0.90", {"start": v(116.1, -15.32) * mm, "end": v(113.6, -13.87) * mm});
            skLineSegment(sketch, "E81.1.0.91", {"start": v(50.6, -13.87) * mm, "end": v(53.1, -15.32) * mm});
            skLineSegment(sketch, "E81.1.0.92", {"start": v(109.1, -15.32) * mm, "end": v(106.6, -13.87) * mm});
            skLineSegment(sketch, "E81.1.0.93", {"start": v(74.16, -15.32) * mm, "end": v(71.63, -13.92) * mm});
            skLineSegment(sketch, "E81.1.0.94", {"start": v(5.47, -7.61) * mm, "end": v(7.97, -9.06) * mm});
            skLineSegment(sketch, "E81.1.0.95", {"start": v(7.97, -3.28) * mm, "end": v(5.47, -4.73) * mm});
            skLineSegment(sketch, "E81.1.0.96", {"start": v(104.6, -10.99) * mm, "end": v(104.6, -13.87) * mm});
            skCircle(sketch, "E81.1.0.97", {"center": v(98.97, -6.17) * mm, "radius": 2.5 * mm, "construction": true});
            skLineSegment(sketch, "E81.1.0.98", {"start": v(108.47, -4.73) * mm, "end": v(108.47, -7.61) * mm});
            skCircle(sketch, "E81.1.0.99", {"center": v(60.1, -12.43) * mm, "radius": 2.5 * mm, "construction": true});
            skLineSegment(sketch, "E81.1.0.100", {"start": v(28.97, -3.28) * mm, "end": v(26.47, -4.73) * mm});
            skLineSegment(sketch, "E81.1.0.101", {"start": v(48.6, -10.99) * mm, "end": v(46.1, -9.54) * mm});
            skLineSegment(sketch, "E81.1.0.102", {"start": v(84.97, -9.06) * mm, "end": v(82.47, -7.61) * mm});
            skLineSegment(sketch, "E81.1.0.103", {"start": v(27.6, -13.87) * mm, "end": v(27.6, -10.99) * mm});
            skLineSegment(sketch, "E81.1.0.104", {"start": v(47.47, -4.73) * mm, "end": v(47.47, -7.61) * mm});
            skLineSegment(sketch, "E81.1.0.105", {"start": v(13.6, -13.87) * mm, "end": v(13.6, -10.99) * mm});
            skLineSegment(sketch, "E81.1.0.106", {"start": v(43.6, -10.99) * mm, "end": v(43.6, -13.87) * mm});
            skCircle(sketch, "E81.1.0.107", {"center": v(53.1, -12.43) * mm, "radius": 2.5 * mm, "construction": true});
            skLineSegment(sketch, "E81.1.0.108", {"start": v(45.47, -7.61) * mm, "end": v(45.47, -4.73) * mm});
            skLineSegment(sketch, "E81.1.0.109", {"start": v(92.6, -13.87) * mm, "end": v(92.6, -10.99) * mm});
            skLineSegment(sketch, "E81.1.0.110", {"start": v(113.6, -13.87) * mm, "end": v(113.6, -10.99) * mm});
            skLineSegment(sketch, "E81.1.0.111", {"start": v(111.6, -10.99) * mm, "end": v(111.6, -13.87) * mm});
            skLineSegment(sketch, "E81.1.0.112", {"start": v(90.6, -10.99) * mm, "end": v(90.6, -13.87) * mm});
            skLineSegment(sketch, "E81.1.0.113", {"start": v(42.97, -3.28) * mm, "end": v(40.47, -4.73) * mm});
            skLineSegment(sketch, "E81.1.0.114", {"start": v(40.47, -4.73) * mm, "end": v(40.47, -7.61) * mm});
            skLineSegment(sketch, "E81.1.0.115", {"start": v(36.6, -13.87) * mm, "end": v(39.1, -15.32) * mm});
            skCircle(sketch, "E81.1.0.116", {"center": v(42.97, -6.17) * mm, "radius": 2.5 * mm, "construction": true});
            skLineSegment(sketch, "E81.1.0.117", {"start": v(66.47, -7.61) * mm, "end": v(63.97, -9.06) * mm});
            skLineSegment(sketch, "E81.1.0.118", {"start": v(14.97, -9.06) * mm, "end": v(17.47, -7.61) * mm});
            skCircle(sketch, "E81.1.0.119", {"center": v(112.97, -6.17) * mm, "radius": 2.5 * mm, "construction": true});
            skLineSegment(sketch, "E81.1.0.120", {"start": v(57.57, -13.83) * mm, "end": v(60.05, -15.32) * mm});
            skCircle(sketch, "E81.1.0.121", {"center": v(77.97, -6.17) * mm, "radius": 2.5 * mm, "construction": true});
            skLineSegment(sketch, "E81.1.0.122", {"start": v(95.1, -15.32) * mm, "end": v(92.6, -13.87) * mm});
            skCircle(sketch, "E81.1.0.123", {"center": v(119.97, -6.17) * mm, "radius": 2.5 * mm, "construction": true});
            skLineSegment(sketch, "E81.1.0.124", {"start": v(35.97, -3.28) * mm, "end": v(33.47, -4.73) * mm});
            skLineSegment(sketch, "E81.1.0.125", {"start": v(82.47, -4.73) * mm, "end": v(84.97, -3.28) * mm});
            skLineSegment(sketch, "E81.1.0.126", {"start": v(45.47, -4.73) * mm, "end": v(42.97, -3.28) * mm});
            skCircle(sketch, "E81.1.0.127", {"center": v(116.1, -12.43) * mm, "radius": 2.5 * mm, "construction": true});
            skLineSegment(sketch, "E81.1.0.128", {"start": v(125.6, -13.87) * mm, "end": v(123.1, -15.32) * mm});
            skLineSegment(sketch, "E81.1.0.129", {"start": v(26.47, -7.61) * mm, "end": v(28.97, -9.06) * mm});
            skLineSegment(sketch, "E81.1.0.130", {"start": v(53.1, -9.54) * mm, "end": v(50.6, -10.99) * mm});
            skLineSegment(sketch, "E81.1.0.131", {"start": v(117.47, -7.61) * mm, "end": v(117.47, -4.73) * mm});
            skLineSegment(sketch, "E81.1.0.132", {"start": v(52.47, -4.73) * mm, "end": v(49.97, -3.28) * mm});
            skLineSegment(sketch, "E81.1.0.133", {"start": v(122.47, -7.61) * mm, "end": v(119.97, -9.06) * mm});
            skLineSegment(sketch, "E81.1.0.134", {"start": v(19.47, -4.73) * mm, "end": v(19.47, -7.61) * mm});
            skLineSegment(sketch, "E81.1.0.135", {"start": v(11.1, -15.32) * mm, "end": v(13.6, -13.87) * mm});
            skLineSegment(sketch, "E81.1.0.136", {"start": v(112.97, -9.06) * mm, "end": v(110.47, -7.61) * mm});
            skLineSegment(sketch, "E81.1.0.137", {"start": v(71.03, -9.06) * mm, "end": v(68.5, -7.66) * mm});
            skLineSegment(sketch, "E81.1.0.138", {"start": v(84.97, -3.28) * mm, "end": v(87.47, -4.73) * mm});
            skLineSegment(sketch, "E81.1.0.139", {"start": v(24.47, -7.61) * mm, "end": v(24.47, -4.73) * mm});
            skLineSegment(sketch, "E81.1.0.140", {"start": v(59.44, -7.66) * mm, "end": v(59.5, -4.78) * mm});
            skLineSegment(sketch, "E81.1.0.141", {"start": v(76.57, -10.94) * mm, "end": v(76.63, -13.83) * mm});
            skLineSegment(sketch, "E81.1.0.142", {"start": v(77.97, -3.28) * mm, "end": v(80.47, -4.73) * mm});
            skLineSegment(sketch, "E81.1.0.143", {"start": v(50.6, -10.99) * mm, "end": v(50.6, -13.87) * mm});
            skLineSegment(sketch, "E81.1.0.144", {"start": v(74.05, -9.54) * mm, "end": v(76.57, -10.94) * mm});
            skLineSegment(sketch, "E81.1.0.145", {"start": v(117.47, -4.73) * mm, "end": v(119.97, -3.28) * mm});
            skLineSegment(sketch, "E81.1.0.146", {"start": v(47.47, -7.61) * mm, "end": v(49.97, -9.06) * mm});
            skLineSegment(sketch, "E81.1.0.147", {"start": v(68.5, -7.66) * mm, "end": v(68.44, -4.78) * mm});
            skLineSegment(sketch, "E81.1.0.148", {"start": v(101.47, -7.61) * mm, "end": v(98.97, -9.06) * mm});
            skLineSegment(sketch, "E81.1.0.149", {"start": v(80.47, -7.61) * mm, "end": v(77.97, -9.06) * mm});
            skLineSegment(sketch, "E81.1.0.150", {"start": v(10.47, -7.61) * mm, "end": v(10.47, -4.73) * mm});
            skLineSegment(sketch, "E81.1.0.151", {"start": v(12.47, -4.73) * mm, "end": v(12.47, -7.61) * mm});
            skLineSegment(sketch, "E81.1.0.152", {"start": v(91.97, -9.06) * mm, "end": v(89.47, -7.61) * mm});
            skLineSegment(sketch, "E81.1.0.153", {"start": v(96.47, -7.61) * mm, "end": v(96.47, -4.73) * mm});
            skLineSegment(sketch, "E81.1.0.154", {"start": v(33.47, -4.73) * mm, "end": v(33.47, -7.61) * mm});
            skLineSegment(sketch, "E81.1.0.155", {"start": v(85.6, -13.87) * mm, "end": v(85.6, -10.99) * mm});
            skLineSegment(sketch, "E81.1.0.156", {"start": v(108.47, -7.61) * mm, "end": v(105.97, -9.06) * mm});
            skLineSegment(sketch, "E81.1.0.157", {"start": v(71.57, -11.04) * mm, "end": v(74.05, -9.54) * mm});
            skLineSegment(sketch, "E81.1.0.158", {"start": v(67.1, -9.54) * mm, "end": v(69.6, -10.99) * mm});
            skLineSegment(sketch, "E81.1.0.159", {"start": v(115.47, -4.73) * mm, "end": v(115.47, -7.61) * mm});
            skLineSegment(sketch, "E81.1.0.160", {"start": v(68.44, -4.78) * mm, "end": v(70.91, -3.29) * mm});
            skLineSegment(sketch, "E81.1.0.161", {"start": v(87.47, -4.73) * mm, "end": v(87.47, -7.61) * mm});
            skLineSegment(sketch, "E81.1.0.162", {"start": v(102.1, -9.54) * mm, "end": v(104.6, -10.99) * mm});
            skLineSegment(sketch, "E81.1.0.163", {"start": v(78.6, -10.99) * mm, "end": v(81.1, -9.54) * mm});
            skLineSegment(sketch, "E81.1.0.164", {"start": v(17.47, -4.73) * mm, "end": v(14.97, -3.28) * mm});
            skLineSegment(sketch, "E81.1.0.165", {"start": v(32.1, -15.32) * mm, "end": v(34.6, -13.87) * mm});
            skLineSegment(sketch, "E81.1.0.166", {"start": v(103.47, -7.61) * mm, "end": v(103.47, -4.73) * mm});
            skLineSegment(sketch, "E81.1.0.167", {"start": v(99.6, -10.99) * mm, "end": v(102.1, -9.54) * mm});
            skLineSegment(sketch, "E81.1.0.168", {"start": v(118.6, -10.99) * mm, "end": v(118.6, -13.87) * mm});
            skLineSegment(sketch, "E81.1.0.169", {"start": v(78.6, -13.87) * mm, "end": v(78.6, -10.99) * mm});
            skLineSegment(sketch, "E81.1.0.170", {"start": v(97.6, -10.99) * mm, "end": v(97.6, -13.87) * mm});
            skLineSegment(sketch, "E81.1.0.171", {"start": v(10.47, -4.73) * mm, "end": v(7.97, -3.28) * mm});
            skLineSegment(sketch, "E81.1.0.172", {"start": v(106.6, -10.99) * mm, "end": v(109.1, -9.54) * mm});
            skLineSegment(sketch, "E81.1.0.173", {"start": v(87.47, -7.61) * mm, "end": v(84.97, -9.06) * mm});
            skLineSegment(sketch, "E81.1.0.174", {"start": v(31.47, -7.61) * mm, "end": v(31.47, -4.73) * mm});
            skLineSegment(sketch, "E81.1.0.175", {"start": v(62.63, -11.04) * mm, "end": v(60.16, -9.54) * mm});
            skLineSegment(sketch, "E81.1.0.176", {"start": v(73.5, -7.57) * mm, "end": v(71.03, -9.06) * mm});
            skLineSegment(sketch, "E81.1.0.177", {"start": v(35.97, -9.06) * mm, "end": v(38.47, -7.61) * mm});
            skLineSegment(sketch, "E81.1.0.178", {"start": v(60.16, -9.54) * mm, "end": v(57.63, -10.94) * mm});
            skLineSegment(sketch, "E81.1.0.179", {"start": v(31.47, -4.73) * mm, "end": v(28.97, -3.28) * mm});
            skLineSegment(sketch, "E81.1.0.180", {"start": v(112.97, -3.28) * mm, "end": v(115.47, -4.73) * mm});
            skLineSegment(sketch, "E81.1.0.181", {"start": v(28.97, -9.06) * mm, "end": v(31.47, -7.61) * mm});
            skLineSegment(sketch, "E81.1.0.182", {"start": v(105.97, -9.06) * mm, "end": v(103.47, -7.61) * mm});
            skLineSegment(sketch, "E81.1.0.183", {"start": v(43.6, -13.87) * mm, "end": v(46.1, -15.32) * mm});
            skLineSegment(sketch, "E81.1.0.184", {"start": v(8.6, -10.99) * mm, "end": v(8.6, -13.87) * mm});
            skLineSegment(sketch, "E81.1.0.185", {"start": v(88.1, -15.32) * mm, "end": v(85.6, -13.87) * mm});
            skLineSegment(sketch, "E81.1.0.186", {"start": v(34.6, -10.99) * mm, "end": v(32.1, -9.54) * mm});
            skLineSegment(sketch, "E81.1.0.187", {"start": v(67.1, -15.32) * mm, "end": v(64.6, -13.87) * mm});
            skLineSegment(sketch, "E81.1.0.188", {"start": v(88.1, -9.54) * mm, "end": v(90.6, -10.99) * mm});
            skLineSegment(sketch, "E81.1.0.189", {"start": v(15.6, -13.87) * mm, "end": v(18.1, -15.32) * mm});
            skLineSegment(sketch, "E81.1.0.190", {"start": v(39.1, -9.54) * mm, "end": v(36.6, -10.99) * mm});
            skLineSegment(sketch, "E81.1.0.191", {"start": v(95.1, -9.54) * mm, "end": v(97.6, -10.99) * mm});
            skLineSegment(sketch, "E81.1.0.192", {"start": v(14.97, -3.28) * mm, "end": v(12.47, -4.73) * mm});
            skLineSegment(sketch, "E81.1.0.193", {"start": v(32.1, -9.54) * mm, "end": v(29.6, -10.99) * mm});
            skLineSegment(sketch, "E81.1.0.194", {"start": v(13.6, -10.99) * mm, "end": v(11.1, -9.54) * mm});
            skLineSegment(sketch, "E81.1.0.195", {"start": v(120.6, -10.99) * mm, "end": v(123.1, -9.54) * mm});
            skLineSegment(sketch, "E81.1.0.196", {"start": v(8.6, -13.87) * mm, "end": v(11.1, -15.32) * mm});
            skLineSegment(sketch, "E81.1.0.197", {"start": v(98.97, -3.28) * mm, "end": v(101.47, -4.73) * mm});
            skLineSegment(sketch, "E81.1.0.198", {"start": v(81.1, -15.32) * mm, "end": v(78.6, -13.87) * mm});
            skLineSegment(sketch, "E81.1.0.199", {"start": v(81.1, -9.54) * mm, "end": v(83.6, -10.99) * mm});
            skLineSegment(sketch, "E81.1.0.200", {"start": v(82.47, -7.61) * mm, "end": v(82.47, -4.73) * mm});
            skLineSegment(sketch, "E81.1.0.201", {"start": v(63.97, -9.06) * mm, "end": v(61.47, -7.61) * mm});
            skLineSegment(sketch, "E81.1.0.202", {"start": v(123.1, -9.54) * mm, "end": v(125.6, -10.99) * mm});
            skLineSegment(sketch, "E81.1.0.203", {"start": v(105.97, -3.28) * mm, "end": v(108.47, -4.73) * mm});
            skLineSegment(sketch, "E81.1.0.204", {"start": v(85.6, -10.99) * mm, "end": v(88.1, -9.54) * mm});
            skLineSegment(sketch, "E81.1.0.205", {"start": v(90.6, -13.87) * mm, "end": v(88.1, -15.32) * mm});
            skLineSegment(sketch, "E81.1.0.206", {"start": v(91.97, -3.28) * mm, "end": v(94.47, -4.73) * mm});
            skLineSegment(sketch, "E81.1.0.207", {"start": v(80.47, -4.73) * mm, "end": v(80.47, -7.61) * mm});
            skLineSegment(sketch, "E81.1.0.208", {"start": v(106.6, -13.87) * mm, "end": v(106.6, -10.99) * mm});
            skLineSegment(sketch, "E81.1.0.209", {"start": v(12.47, -7.61) * mm, "end": v(14.97, -9.06) * mm});
            skLineSegment(sketch, "E81.1.0.210", {"start": v(59.5, -4.78) * mm, "end": v(57.03, -3.29) * mm});
            skLineSegment(sketch, "E81.1.0.211", {"start": v(119.97, -9.06) * mm, "end": v(117.47, -7.61) * mm});
            skLineSegment(sketch, "E81.1.0.212", {"start": v(89.47, -7.61) * mm, "end": v(89.47, -4.73) * mm});
            skLineSegment(sketch, "E81.1.0.213", {"start": v(109.1, -9.54) * mm, "end": v(111.6, -10.99) * mm});
            skLineSegment(sketch, "E81.1.0.214", {"start": v(41.6, -13.87) * mm, "end": v(41.6, -10.99) * mm});
            skLineSegment(sketch, "E81.1.0.215", {"start": v(123.1, -15.32) * mm, "end": v(120.6, -13.87) * mm});
            skLineSegment(sketch, "E81.1.0.216", {"start": v(29.6, -10.99) * mm, "end": v(29.6, -13.87) * mm});
            skLineSegment(sketch, "E81.1.0.217", {"start": v(89.47, -4.73) * mm, "end": v(91.97, -3.28) * mm});
            skLineSegment(sketch, "E81.1.0.218", {"start": v(104.6, -13.87) * mm, "end": v(102.1, -15.32) * mm});
            skLineSegment(sketch, "E81.1.0.219", {"start": v(113.6, -10.99) * mm, "end": v(116.1, -9.54) * mm});
            skLineSegment(sketch, "E81.1.0.220", {"start": v(92.6, -10.99) * mm, "end": v(95.1, -9.54) * mm});
            skLineSegment(sketch, "E81.1.0.221", {"start": v(77.97, -9.06) * mm, "end": v(75.47, -7.61) * mm});
            skLineSegment(sketch, "E81.1.0.222", {"start": v(7.97, -9.06) * mm, "end": v(10.47, -7.61) * mm});
            skLineSegment(sketch, "E81.1.0.223", {"start": v(83.6, -13.87) * mm, "end": v(81.1, -15.32) * mm});
            skLineSegment(sketch, "E81.1.0.224", {"start": v(52.47, -7.61) * mm, "end": v(52.47, -4.73) * mm});
            skLineSegment(sketch, "E81.1.0.225", {"start": v(54.5, -4.68) * mm, "end": v(54.44, -7.57) * mm});
            skLineSegment(sketch, "E81.1.0.226", {"start": v(61.47, -4.73) * mm, "end": v(63.97, -3.28) * mm});
            skLineSegment(sketch, "E81.1.0.227", {"start": v(18.1, -15.32) * mm, "end": v(20.6, -13.87) * mm});
            skLineSegment(sketch, "E81.1.0.228", {"start": v(55.6, -10.99) * mm, "end": v(53.1, -9.54) * mm});
            skLineSegment(sketch, "E81.1.0.229", {"start": v(110.47, -4.73) * mm, "end": v(112.97, -3.28) * mm});
            skLineSegment(sketch, "E81.1.0.230", {"start": v(83.6, -10.99) * mm, "end": v(83.6, -13.87) * mm});
            skLineSegment(sketch, "E81.1.0.231", {"start": v(66.47, -4.73) * mm, "end": v(66.47, -7.61) * mm});
            skLineSegment(sketch, "E81.1.0.232", {"start": v(98.97, -9.06) * mm, "end": v(96.47, -7.61) * mm});
            skLineSegment(sketch, "E81.1.0.233", {"start": v(62.57, -13.92) * mm, "end": v(62.63, -11.04) * mm});
            skLineSegment(sketch, "E81.1.0.234", {"start": v(39.1, -15.32) * mm, "end": v(41.6, -13.87) * mm});
            skLineSegment(sketch, "E81.1.0.235", {"start": v(94.47, -7.61) * mm, "end": v(91.97, -9.06) * mm});
            skLineSegment(sketch, "E81.1.0.236", {"start": v(22.6, -13.87) * mm, "end": v(25.1, -15.32) * mm});
            skLineSegment(sketch, "E81.1.0.237", {"start": v(38.47, -4.73) * mm, "end": v(35.97, -3.28) * mm});
            skLineSegment(sketch, "E81.1.0.238", {"start": v(96.47, -4.73) * mm, "end": v(98.97, -3.28) * mm});
            skLineSegment(sketch, "E81.2.0.0", {"start": v(24.2, -17.16) * mm, "end": v(21.7, -15.72) * mm});
            skLineSegment(sketch, "E81.2.0.1", {"start": v(75.2, -17.16) * mm, "end": v(77.7, -15.72) * mm});
            skLineSegment(sketch, "E81.2.0.2", {"start": v(54.17, -20) * mm, "end": v(56.64, -21.49) * mm});
            skLineSegment(sketch, "E81.2.0.3", {"start": v(48.33, -26.3) * mm, "end": v(48.33, -23.42) * mm});
            skLineSegment(sketch, "E81.2.0.4", {"start": v(20.33, -23.42) * mm, "end": v(17.83, -21.98) * mm});
            skCircle(sketch, "E81.2.0.5", {"center": v(35.7, -18.6) * mm, "radius": 2.5 * mm, "construction": true});
            skCircle(sketch, "E81.2.0.7", {"center": v(63.7, -18.6) * mm, "radius": 2.5 * mm, "construction": true});
            skLineSegment(sketch, "E81.2.0.8", {"start": v(20.33, -26.3) * mm, "end": v(20.33, -23.42) * mm});
            skCircle(sketch, "E81.2.0.9", {"center": v(28.7, -18.6) * mm, "radius": 2.5 * mm, "construction": true});
            skCircle(sketch, "E81.2.0.10", {"center": v(70.7, -18.6) * mm, "radius": 2.5 * mm, "construction": true});
            skLineSegment(sketch, "E81.2.0.11", {"start": v(110.2, -20.05) * mm, "end": v(110.2, -17.16) * mm});
            skLineSegment(sketch, "E81.2.0.12", {"start": v(61.2, -20.05) * mm, "end": v(61.2, -17.16) * mm});
            skLineSegment(sketch, "E81.2.0.13", {"start": v(94.2, -17.16) * mm, "end": v(94.2, -20.05) * mm});
            skLineSegment(sketch, "E81.2.0.14", {"start": v(5.2, -17.16) * mm, "end": v(5.2, -20.05) * mm});
            skLineSegment(sketch, "E81.2.0.15", {"start": v(8.33, -26.3) * mm, "end": v(5.2, -20.05) * mm, "construction": true});
            skLineSegment(sketch, "E81.2.0.16", {"start": v(56.64, -21.49) * mm, "end": v(59.17, -20.1) * mm});
            skCircle(sketch, "E81.2.0.17", {"center": v(10.83, -24.86) * mm, "radius": 2.5 * mm, "construction": true});
            skLineSegment(sketch, "E81.2.0.18", {"start": v(40.2, -20.05) * mm, "end": v(42.7, -21.49) * mm});
            skLineSegment(sketch, "E81.2.0.19", {"start": v(103.2, -17.16) * mm, "end": v(105.7, -15.72) * mm});
            skCircle(sketch, "E81.2.0.20", {"center": v(14.7, -18.6) * mm, "radius": 2.5 * mm, "construction": true});
            skCircle(sketch, "E81.2.0.23", {"center": v(108.83, -24.86) * mm, "radius": 2.5 * mm, "construction": true});
            skLineSegment(sketch, "E81.2.0.24", {"start": v(73.17, -17.11) * mm, "end": v(73.23, -20) * mm});
            skCircle(sketch, "E81.2.0.26", {"center": v(84.7, -18.6) * mm, "radius": 2.5 * mm, "construction": true});
            skLineSegment(sketch, "E81.2.0.27", {"start": v(21.7, -15.72) * mm, "end": v(19.2, -17.16) * mm});
            skCircle(sketch, "E81.2.0.28", {"center": v(105.7, -18.6) * mm, "radius": 2.5 * mm, "construction": true});
            skLineSegment(sketch, "E81.2.0.29", {"start": v(42.7, -21.49) * mm, "end": v(45.2, -20.05) * mm});
            skLineSegment(sketch, "E81.2.0.30", {"start": v(36.33, -23.42) * mm, "end": v(36.33, -26.3) * mm});
            skCircle(sketch, "E81.2.0.31", {"center": v(73.83, -24.86) * mm, "radius": 2.5 * mm, "construction": true});
            skLineSegment(sketch, "E81.2.0.32", {"start": v(64.33, -23.42) * mm, "end": v(66.83, -21.98) * mm});
            skLineSegment(sketch, "E81.2.0.33", {"start": v(64.33, -26.3) * mm, "end": v(64.33, -23.42) * mm});
            skCircle(sketch, "E81.2.0.34", {"center": v(91.7, -18.6) * mm, "radius": 2.5 * mm, "construction": true});
            skCircle(sketch, "E81.2.0.35", {"center": v(56.7, -18.6) * mm, "radius": 2.5 * mm, "construction": true});
            skCircle(sketch, "E81.2.0.36", {"center": v(24.83, -24.86) * mm, "radius": 2.5 * mm, "construction": true});
            skLineSegment(sketch, "E81.2.0.37", {"start": v(15.33, -23.42) * mm, "end": v(15.33, -26.3) * mm});
            skLineSegment(sketch, "E81.2.0.38", {"start": v(34.33, -26.3) * mm, "end": v(34.33, -23.42) * mm});
            skCircle(sketch, "E81.2.0.40", {"center": v(87.83, -24.86) * mm, "radius": 2.5 * mm, "construction": true});
            skLineSegment(sketch, "E81.2.0.41", {"start": v(10.83, -21.98) * mm, "end": v(8.33, -23.42) * mm});
            skCircle(sketch, "E81.2.0.42", {"center": v(45.83, -24.86) * mm, "radius": 2.5 * mm, "construction": true});
            skLineSegment(sketch, "E81.2.0.43", {"start": v(99.33, -26.3) * mm, "end": v(99.33, -23.42) * mm});
            skLineSegment(sketch, "E81.2.0.44", {"start": v(49.7, -15.72) * mm, "end": v(47.2, -17.16) * mm});
            skLineSegment(sketch, "E81.2.0.45", {"start": v(115.2, -20.05) * mm, "end": v(112.7, -21.49) * mm});
            skLineSegment(sketch, "E81.2.0.46", {"start": v(19.2, -20.05) * mm, "end": v(21.7, -21.49) * mm});
            skLineSegment(sketch, "E81.2.0.47", {"start": v(119.7, -15.72) * mm, "end": v(122.2, -17.16) * mm});
            skLineSegment(sketch, "E81.2.0.48", {"start": v(21.7, -21.49) * mm, "end": v(24.2, -20.05) * mm});
            skLineSegment(sketch, "E81.2.0.49", {"start": v(122.2, -17.16) * mm, "end": v(122.2, -20.05) * mm});
            skCircle(sketch, "E81.2.0.51", {"center": v(17.83, -24.86) * mm, "radius": 2.5 * mm, "construction": true});
            skLineSegment(sketch, "E81.2.0.52", {"start": v(57.36, -23.37) * mm, "end": v(57.3, -26.26) * mm});
            skCircle(sketch, "E81.2.0.53", {"center": v(80.83, -24.86) * mm, "radius": 2.5 * mm, "construction": true});
            skCircle(sketch, "E81.2.0.54", {"center": v(21.7, -18.6) * mm, "radius": 2.5 * mm, "construction": true});
            skLineSegment(sketch, "E81.2.0.55", {"start": v(55.33, -26.3) * mm, "end": v(55.33, -23.42) * mm});
            skLineSegment(sketch, "E81.2.0.56", {"start": v(27.33, -23.42) * mm, "end": v(24.83, -21.98) * mm});
            skCircle(sketch, "E81.2.0.57", {"center": v(122.83, -24.86) * mm, "radius": 2.5 * mm, "construction": true});
            skCircle(sketch, "E81.2.0.58", {"center": v(7.7, -18.6) * mm, "radius": 2.5 * mm, "construction": true});
            skLineSegment(sketch, "E81.2.0.59", {"start": v(22.33, -23.42) * mm, "end": v(22.33, -26.3) * mm});
            skLineSegment(sketch, "E81.2.0.60", {"start": v(56.75, -15.72) * mm, "end": v(54.23, -17.11) * mm});
            skLineSegment(sketch, "E81.2.0.61", {"start": v(26.2, -17.16) * mm, "end": v(26.2, -20.05) * mm});
            skLineSegment(sketch, "E81.2.0.62", {"start": v(75.2, -20.05) * mm, "end": v(75.2, -17.16) * mm});
            skLineSegment(sketch, "E81.2.0.63", {"start": v(38.2, -20.05) * mm, "end": v(38.2, -17.16) * mm});
            skLineSegment(sketch, "E81.2.0.64", {"start": v(115.83, -21.98) * mm, "end": v(118.33, -23.42) * mm});
            skLineSegment(sketch, "E81.2.0.65", {"start": v(125.33, -23.42) * mm, "end": v(125.33, -26.3) * mm});
            skCircle(sketch, "E81.2.0.66", {"center": v(49.7, -18.6) * mm, "radius": 2.5 * mm, "construction": true});
            skCircle(sketch, "E81.2.0.67", {"center": v(101.83, -24.86) * mm, "radius": 2.5 * mm, "construction": true});
            skCircle(sketch, "E81.2.0.68", {"center": v(66.83, -24.86) * mm, "radius": 2.5 * mm, "construction": true});
            skLineSegment(sketch, "E81.2.0.69", {"start": v(69.33, -23.42) * mm, "end": v(69.33, -26.3) * mm});
            skCircle(sketch, "E81.2.0.72", {"center": v(31.83, -24.86) * mm, "radius": 2.5 * mm, "construction": true});
            skLineSegment(sketch, "E81.2.0.73", {"start": v(120.33, -26.3) * mm, "end": v(120.33, -23.42) * mm});
            skCircle(sketch, "E81.2.0.74", {"center": v(38.83, -24.86) * mm, "radius": 2.5 * mm, "construction": true});
            skLineSegment(sketch, "E81.2.0.77", {"start": v(71.36, -26.35) * mm, "end": v(71.3, -23.47) * mm});
            skLineSegment(sketch, "E81.2.0.78", {"start": v(17.83, -21.98) * mm, "end": v(15.33, -23.42) * mm});
            skLineSegment(sketch, "E81.2.0.79", {"start": v(41.33, -23.42) * mm, "end": v(38.83, -21.98) * mm});
            skLineSegment(sketch, "E81.2.0.80", {"start": v(45.83, -21.98) * mm, "end": v(43.33, -23.42) * mm});
            skLineSegment(sketch, "E81.2.0.81", {"start": v(63.7, -15.72) * mm, "end": v(66.2, -17.16) * mm});
            skLineSegment(sketch, "E81.2.0.82", {"start": v(49.7, -21.49) * mm, "end": v(52.2, -20.05) * mm});
            skLineSegment(sketch, "E81.2.0.83", {"start": v(17.2, -20.05) * mm, "end": v(17.2, -17.16) * mm});
            skLineSegment(sketch, "E81.2.0.85", {"start": v(24.83, -21.98) * mm, "end": v(22.33, -23.42) * mm});
            skLineSegment(sketch, "E81.2.0.86", {"start": v(33.2, -20.05) * mm, "end": v(35.7, -21.49) * mm});
            skCircle(sketch, "E81.2.0.87", {"center": v(94.83, -24.86) * mm, "radius": 2.5 * mm, "construction": true});
            skLineSegment(sketch, "E81.2.0.88", {"start": v(101.2, -17.16) * mm, "end": v(101.2, -20.05) * mm});
            skLineSegment(sketch, "E81.2.0.89", {"start": v(70.64, -15.72) * mm, "end": v(73.17, -17.11) * mm});
            skLineSegment(sketch, "E81.2.0.94", {"start": v(5.2, -20.05) * mm, "end": v(7.7, -21.49) * mm});
            skLineSegment(sketch, "E81.2.0.95", {"start": v(7.7, -15.72) * mm, "end": v(5.2, -17.16) * mm});
            skLineSegment(sketch, "E81.2.0.96", {"start": v(104.33, -23.42) * mm, "end": v(104.33, -26.3) * mm});
            skCircle(sketch, "E81.2.0.97", {"center": v(98.7, -18.6) * mm, "radius": 2.5 * mm, "construction": true});
            skLineSegment(sketch, "E81.2.0.98", {"start": v(108.2, -17.16) * mm, "end": v(108.2, -20.05) * mm});
            skCircle(sketch, "E81.2.0.99", {"center": v(59.83, -24.86) * mm, "radius": 2.5 * mm, "construction": true});
            skLineSegment(sketch, "E81.2.0.100", {"start": v(28.7, -15.72) * mm, "end": v(26.2, -17.16) * mm});
            skLineSegment(sketch, "E81.2.0.101", {"start": v(48.33, -23.42) * mm, "end": v(45.83, -21.98) * mm});
            skLineSegment(sketch, "E81.2.0.102", {"start": v(84.7, -21.49) * mm, "end": v(82.2, -20.05) * mm});
            skLineSegment(sketch, "E81.2.0.103", {"start": v(27.33, -26.3) * mm, "end": v(27.33, -23.42) * mm});
            skLineSegment(sketch, "E81.2.0.104", {"start": v(47.2, -17.16) * mm, "end": v(47.2, -20.05) * mm});
            skLineSegment(sketch, "E81.2.0.105", {"start": v(13.33, -26.3) * mm, "end": v(13.33, -23.42) * mm});
            skLineSegment(sketch, "E81.2.0.106", {"start": v(43.33, -23.42) * mm, "end": v(43.33, -26.3) * mm});
            skCircle(sketch, "E81.2.0.107", {"center": v(52.83, -24.86) * mm, "radius": 2.5 * mm, "construction": true});
            skLineSegment(sketch, "E81.2.0.108", {"start": v(45.2, -20.05) * mm, "end": v(45.2, -17.16) * mm});
            skLineSegment(sketch, "E81.2.0.109", {"start": v(92.33, -26.3) * mm, "end": v(92.33, -23.42) * mm});
            skLineSegment(sketch, "E81.2.0.110", {"start": v(113.33, -26.3) * mm, "end": v(113.33, -23.42) * mm});
            skLineSegment(sketch, "E81.2.0.111", {"start": v(111.33, -23.42) * mm, "end": v(111.33, -26.3) * mm});
            skLineSegment(sketch, "E81.2.0.112", {"start": v(90.33, -23.42) * mm, "end": v(90.33, -26.3) * mm});
            skLineSegment(sketch, "E81.2.0.113", {"start": v(42.7, -15.72) * mm, "end": v(40.2, -17.16) * mm});
            skLineSegment(sketch, "E81.2.0.114", {"start": v(40.2, -17.16) * mm, "end": v(40.2, -20.05) * mm});
            skCircle(sketch, "E81.2.0.116", {"center": v(42.7, -18.6) * mm, "radius": 2.5 * mm, "construction": true});
            skLineSegment(sketch, "E81.2.0.117", {"start": v(66.2, -20.05) * mm, "end": v(63.7, -21.49) * mm});
            skLineSegment(sketch, "E81.2.0.118", {"start": v(14.7, -21.49) * mm, "end": v(17.2, -20.05) * mm});
            skCircle(sketch, "E81.2.0.119", {"center": v(112.7, -18.6) * mm, "radius": 2.5 * mm, "construction": true});
            skCircle(sketch, "E81.2.0.121", {"center": v(77.7, -18.6) * mm, "radius": 2.5 * mm, "construction": true});
            skCircle(sketch, "E81.2.0.123", {"center": v(119.7, -18.6) * mm, "radius": 2.5 * mm, "construction": true});
            skLineSegment(sketch, "E81.2.0.124", {"start": v(35.7, -15.72) * mm, "end": v(33.2, -17.16) * mm});
            skLineSegment(sketch, "E81.2.0.125", {"start": v(82.2, -17.16) * mm, "end": v(84.7, -15.72) * mm});
            skLineSegment(sketch, "E81.2.0.126", {"start": v(45.2, -17.16) * mm, "end": v(42.7, -15.72) * mm});
            skCircle(sketch, "E81.2.0.127", {"center": v(115.83, -24.86) * mm, "radius": 2.5 * mm, "construction": true});
            skLineSegment(sketch, "E81.2.0.129", {"start": v(26.2, -20.05) * mm, "end": v(28.7, -21.49) * mm});
            skLineSegment(sketch, "E81.2.0.130", {"start": v(52.83, -21.98) * mm, "end": v(50.33, -23.42) * mm});
            skLineSegment(sketch, "E81.2.0.131", {"start": v(117.2, -20.05) * mm, "end": v(117.2, -17.16) * mm});
            skLineSegment(sketch, "E81.2.0.132", {"start": v(52.2, -17.16) * mm, "end": v(49.7, -15.72) * mm});
            skLineSegment(sketch, "E81.2.0.133", {"start": v(122.2, -20.05) * mm, "end": v(119.7, -21.49) * mm});
            skLineSegment(sketch, "E81.2.0.134", {"start": v(19.2, -17.16) * mm, "end": v(19.2, -20.05) * mm});
            skLineSegment(sketch, "E81.2.0.136", {"start": v(112.7, -21.49) * mm, "end": v(110.2, -20.05) * mm});
            skLineSegment(sketch, "E81.2.0.137", {"start": v(70.75, -21.49) * mm, "end": v(68.23, -20.1) * mm});
            skLineSegment(sketch, "E81.2.0.138", {"start": v(84.7, -15.72) * mm, "end": v(87.2, -17.16) * mm});
            skLineSegment(sketch, "E81.2.0.139", {"start": v(24.2, -20.05) * mm, "end": v(24.2, -17.16) * mm});
            skLineSegment(sketch, "E81.2.0.140", {"start": v(59.17, -20.1) * mm, "end": v(59.23, -17.2) * mm});
            skLineSegment(sketch, "E81.2.0.141", {"start": v(76.3, -23.37) * mm, "end": v(76.36, -26.26) * mm});
            skLineSegment(sketch, "E81.2.0.142", {"start": v(77.7, -15.72) * mm, "end": v(80.2, -17.16) * mm});
            skLineSegment(sketch, "E81.2.0.143", {"start": v(50.33, -23.42) * mm, "end": v(50.33, -26.3) * mm});
            skLineSegment(sketch, "E81.2.0.144", {"start": v(73.77, -21.98) * mm, "end": v(76.3, -23.37) * mm});
            skLineSegment(sketch, "E81.2.0.145", {"start": v(117.2, -17.16) * mm, "end": v(119.7, -15.72) * mm});
            skLineSegment(sketch, "E81.2.0.146", {"start": v(47.2, -20.05) * mm, "end": v(49.7, -21.49) * mm});
            skLineSegment(sketch, "E81.2.0.147", {"start": v(68.23, -20.1) * mm, "end": v(68.17, -17.2) * mm});
            skLineSegment(sketch, "E81.2.0.148", {"start": v(101.2, -20.05) * mm, "end": v(98.7, -21.49) * mm});
            skLineSegment(sketch, "E81.2.0.149", {"start": v(80.2, -20.05) * mm, "end": v(77.7, -21.49) * mm});
            skLineSegment(sketch, "E81.2.0.150", {"start": v(10.2, -20.05) * mm, "end": v(10.2, -17.16) * mm});
            skLineSegment(sketch, "E81.2.0.151", {"start": v(12.2, -17.16) * mm, "end": v(12.2, -20.05) * mm});
            skLineSegment(sketch, "E81.2.0.152", {"start": v(91.7, -21.49) * mm, "end": v(89.2, -20.05) * mm});
            skLineSegment(sketch, "E81.2.0.153", {"start": v(96.2, -20.05) * mm, "end": v(96.2, -17.16) * mm});
            skLineSegment(sketch, "E81.2.0.154", {"start": v(33.2, -17.16) * mm, "end": v(33.2, -20.05) * mm});
            skLineSegment(sketch, "E81.2.0.155", {"start": v(85.33, -26.3) * mm, "end": v(85.33, -23.42) * mm});
            skLineSegment(sketch, "E81.2.0.156", {"start": v(108.2, -20.05) * mm, "end": v(105.7, -21.49) * mm});
            skLineSegment(sketch, "E81.2.0.157", {"start": v(71.3, -23.47) * mm, "end": v(73.77, -21.98) * mm});
            skLineSegment(sketch, "E81.2.0.158", {"start": v(66.83, -21.98) * mm, "end": v(69.33, -23.42) * mm});
            skLineSegment(sketch, "E81.2.0.159", {"start": v(115.2, -17.16) * mm, "end": v(115.2, -20.05) * mm});
            skLineSegment(sketch, "E81.2.0.160", {"start": v(68.17, -17.2) * mm, "end": v(70.64, -15.72) * mm});
            skLineSegment(sketch, "E81.2.0.161", {"start": v(87.2, -17.16) * mm, "end": v(87.2, -20.05) * mm});
            skLineSegment(sketch, "E81.2.0.162", {"start": v(101.83, -21.98) * mm, "end": v(104.33, -23.42) * mm});
            skLineSegment(sketch, "E81.2.0.163", {"start": v(78.33, -23.42) * mm, "end": v(80.83, -21.98) * mm});
            skLineSegment(sketch, "E81.2.0.164", {"start": v(17.2, -17.16) * mm, "end": v(14.7, -15.72) * mm});
            skLineSegment(sketch, "E81.2.0.166", {"start": v(103.2, -20.05) * mm, "end": v(103.2, -17.16) * mm});
            skLineSegment(sketch, "E81.2.0.167", {"start": v(99.33, -23.42) * mm, "end": v(101.83, -21.98) * mm});
            skLineSegment(sketch, "E81.2.0.168", {"start": v(118.33, -23.42) * mm, "end": v(118.33, -26.3) * mm});
            skLineSegment(sketch, "E81.2.0.169", {"start": v(78.33, -26.3) * mm, "end": v(78.33, -23.42) * mm});
            skLineSegment(sketch, "E81.2.0.170", {"start": v(97.33, -23.42) * mm, "end": v(97.33, -26.3) * mm});
            skLineSegment(sketch, "E81.2.0.171", {"start": v(10.2, -17.16) * mm, "end": v(7.7, -15.72) * mm});
            skLineSegment(sketch, "E81.2.0.172", {"start": v(106.33, -23.42) * mm, "end": v(108.83, -21.98) * mm});
            skLineSegment(sketch, "E81.2.0.173", {"start": v(87.2, -20.05) * mm, "end": v(84.7, -21.49) * mm});
            skLineSegment(sketch, "E81.2.0.174", {"start": v(31.2, -20.05) * mm, "end": v(31.2, -17.16) * mm});
            skLineSegment(sketch, "E81.2.0.175", {"start": v(62.36, -23.47) * mm, "end": v(59.89, -21.98) * mm});
            skLineSegment(sketch, "E81.2.0.176", {"start": v(73.23, -20) * mm, "end": v(70.75, -21.49) * mm});
            skLineSegment(sketch, "E81.2.0.177", {"start": v(35.7, -21.49) * mm, "end": v(38.2, -20.05) * mm});
            skLineSegment(sketch, "E81.2.0.178", {"start": v(59.89, -21.98) * mm, "end": v(57.36, -23.37) * mm});
            skLineSegment(sketch, "E81.2.0.179", {"start": v(31.2, -17.16) * mm, "end": v(28.7, -15.72) * mm});
            skLineSegment(sketch, "E81.2.0.180", {"start": v(112.7, -15.72) * mm, "end": v(115.2, -17.16) * mm});
            skLineSegment(sketch, "E81.2.0.181", {"start": v(28.7, -21.49) * mm, "end": v(31.2, -20.05) * mm});
            skLineSegment(sketch, "E81.2.0.182", {"start": v(105.7, -21.49) * mm, "end": v(103.2, -20.05) * mm});
            skLineSegment(sketch, "E81.2.0.184", {"start": v(8.33, -23.42) * mm, "end": v(8.33, -26.3) * mm});
            skLineSegment(sketch, "E81.2.0.186", {"start": v(34.33, -23.42) * mm, "end": v(31.83, -21.98) * mm});
            skLineSegment(sketch, "E81.2.0.188", {"start": v(87.83, -21.98) * mm, "end": v(90.33, -23.42) * mm});
            skLineSegment(sketch, "E81.2.0.190", {"start": v(38.83, -21.98) * mm, "end": v(36.33, -23.42) * mm});
            skLineSegment(sketch, "E81.2.0.191", {"start": v(94.83, -21.98) * mm, "end": v(97.33, -23.42) * mm});
            skLineSegment(sketch, "E81.2.0.192", {"start": v(14.7, -15.72) * mm, "end": v(12.2, -17.16) * mm});
            skLineSegment(sketch, "E81.2.0.193", {"start": v(31.83, -21.98) * mm, "end": v(29.33, -23.42) * mm});
            skLineSegment(sketch, "E81.2.0.194", {"start": v(13.33, -23.42) * mm, "end": v(10.83, -21.98) * mm});
            skLineSegment(sketch, "E81.2.0.195", {"start": v(120.33, -23.42) * mm, "end": v(122.83, -21.98) * mm});
            skLineSegment(sketch, "E81.2.0.197", {"start": v(98.7, -15.72) * mm, "end": v(101.2, -17.16) * mm});
            skLineSegment(sketch, "E81.2.0.199", {"start": v(80.83, -21.98) * mm, "end": v(83.33, -23.42) * mm});
            skLineSegment(sketch, "E81.2.0.200", {"start": v(82.2, -20.05) * mm, "end": v(82.2, -17.16) * mm});
            skLineSegment(sketch, "E81.2.0.201", {"start": v(63.7, -21.49) * mm, "end": v(61.2, -20.05) * mm});
            skLineSegment(sketch, "E81.2.0.202", {"start": v(122.83, -21.98) * mm, "end": v(125.33, -23.42) * mm});
            skLineSegment(sketch, "E81.2.0.203", {"start": v(105.7, -15.72) * mm, "end": v(108.2, -17.16) * mm});
            skLineSegment(sketch, "E81.2.0.204", {"start": v(85.33, -23.42) * mm, "end": v(87.83, -21.98) * mm});
            skLineSegment(sketch, "E81.2.0.206", {"start": v(91.7, -15.72) * mm, "end": v(94.2, -17.16) * mm});
            skLineSegment(sketch, "E81.2.0.207", {"start": v(80.2, -17.16) * mm, "end": v(80.2, -20.05) * mm});
            skLineSegment(sketch, "E81.2.0.208", {"start": v(106.33, -26.3) * mm, "end": v(106.33, -23.42) * mm});
            skLineSegment(sketch, "E81.2.0.209", {"start": v(12.2, -20.05) * mm, "end": v(14.7, -21.49) * mm});
            skLineSegment(sketch, "E81.2.0.210", {"start": v(59.23, -17.2) * mm, "end": v(56.75, -15.72) * mm});
            skLineSegment(sketch, "E81.2.0.211", {"start": v(119.7, -21.49) * mm, "end": v(117.2, -20.05) * mm});
            skLineSegment(sketch, "E81.2.0.212", {"start": v(89.2, -20.05) * mm, "end": v(89.2, -17.16) * mm});
            skLineSegment(sketch, "E81.2.0.213", {"start": v(108.83, -21.98) * mm, "end": v(111.33, -23.42) * mm});
            skLineSegment(sketch, "E81.2.0.214", {"start": v(41.33, -26.3) * mm, "end": v(41.33, -23.42) * mm});
            skLineSegment(sketch, "E81.2.0.216", {"start": v(29.33, -23.42) * mm, "end": v(29.33, -26.3) * mm});
            skLineSegment(sketch, "E81.2.0.217", {"start": v(89.2, -17.16) * mm, "end": v(91.7, -15.72) * mm});
            skLineSegment(sketch, "E81.2.0.219", {"start": v(113.33, -23.42) * mm, "end": v(115.83, -21.98) * mm});
            skLineSegment(sketch, "E81.2.0.220", {"start": v(92.33, -23.42) * mm, "end": v(94.83, -21.98) * mm});
            skLineSegment(sketch, "E81.2.0.221", {"start": v(77.7, -21.49) * mm, "end": v(75.2, -20.05) * mm});
            skLineSegment(sketch, "E81.2.0.222", {"start": v(7.7, -21.49) * mm, "end": v(10.2, -20.05) * mm});
            skLineSegment(sketch, "E81.2.0.224", {"start": v(52.2, -20.05) * mm, "end": v(52.2, -17.16) * mm});
            skLineSegment(sketch, "E81.2.0.225", {"start": v(54.23, -17.11) * mm, "end": v(54.17, -20) * mm});
            skLineSegment(sketch, "E81.2.0.226", {"start": v(61.2, -17.16) * mm, "end": v(63.7, -15.72) * mm});
            skLineSegment(sketch, "E81.2.0.228", {"start": v(55.33, -23.42) * mm, "end": v(52.83, -21.98) * mm});
            skLineSegment(sketch, "E81.2.0.229", {"start": v(110.2, -17.16) * mm, "end": v(112.7, -15.72) * mm});
            skLineSegment(sketch, "E81.2.0.230", {"start": v(83.33, -23.42) * mm, "end": v(83.33, -26.3) * mm});
            skLineSegment(sketch, "E81.2.0.231", {"start": v(66.2, -17.16) * mm, "end": v(66.2, -20.05) * mm});
            skLineSegment(sketch, "E81.2.0.232", {"start": v(98.7, -21.49) * mm, "end": v(96.2, -20.05) * mm});
            skLineSegment(sketch, "E81.2.0.233", {"start": v(62.3, -26.35) * mm, "end": v(62.36, -23.47) * mm});
            skLineSegment(sketch, "E81.2.0.235", {"start": v(94.2, -20.05) * mm, "end": v(91.7, -21.49) * mm});
            skLineSegment(sketch, "E81.2.0.237", {"start": v(38.2, -17.16) * mm, "end": v(35.7, -15.72) * mm});
            skLineSegment(sketch, "E81.2.0.238", {"start": v(96.2, -17.16) * mm, "end": v(98.7, -15.72) * mm});
            skLineSegment(sketch, "E81.direction1", {"start": v(8.88, -1.44) * mm, "end": v(8.6, -13.87) * mm, "construction": true});
            skLineSegment(sketch, "E82", {"start": v(9.53, 23.42) * mm, "end": v(14.53, 23.42) * mm});
            skLineSegment(sketch, "E83", {"start": v(16.53, 23.42) * mm, "end": v(21.53, 23.42) * mm});
            skLineSegment(sketch, "E84", {"start": v(23.53, 23.42) * mm, "end": v(28.53, 23.42) * mm});
            skLineSegment(sketch, "E85", {"start": v(30.53, 23.42) * mm, "end": v(35.53, 23.42) * mm});
            skLineSegment(sketch, "E86", {"start": v(37.53, 23.42) * mm, "end": v(42.53, 23.42) * mm});
            skLineSegment(sketch, "E87", {"start": v(44.53, 23.42) * mm, "end": v(49.53, 23.42) * mm});
            skLineSegment(sketch, "E88", {"start": v(51.53, 23.42) * mm, "end": v(56.53, 23.42) * mm});
            skLineSegment(sketch, "E89", {"start": v(58.5, 23.47) * mm, "end": v(63.5, 23.37) * mm});
            skLineSegment(sketch, "E90", {"start": v(65.53, 23.42) * mm, "end": v(70.53, 23.42) * mm});
            skLineSegment(sketch, "E91", {"start": v(72.56, 23.37) * mm, "end": v(77.56, 23.47) * mm});
            skLineSegment(sketch, "E92", {"start": v(79.53, 23.42) * mm, "end": v(84.53, 23.42) * mm});
            skLineSegment(sketch, "E93", {"start": v(86.53, 23.42) * mm, "end": v(91.53, 23.42) * mm});
            skLineSegment(sketch, "E94", {"start": v(93.53, 23.42) * mm, "end": v(98.53, 23.42) * mm});
            skLineSegment(sketch, "E95", {"start": v(100.53, 23.42) * mm, "end": v(105.53, 23.42) * mm});
            skLineSegment(sketch, "E96", {"start": v(107.53, 23.42) * mm, "end": v(112.53, 23.42) * mm});
            skLineSegment(sketch, "E97", {"start": v(114.53, 23.42) * mm, "end": v(119.53, 23.42) * mm});
            skLineSegment(sketch, "E98", {"start": v(121.53, 23.42) * mm, "end": v(126.53, 23.42) * mm});
            skLineSegment(sketch, "E99", {"start": v(8.57, 21.58) * mm, "end": v(8.57, 15.8) * mm});
            skLineSegment(sketch, "E100", {"start": v(8.24, 9.15) * mm, "end": v(8.24, 3.37) * mm});
            skLineSegment(sketch, "E101", {"start": v(7.97, -3.28) * mm, "end": v(7.97, -9.06) * mm});
            skLineSegment(sketch, "E102", {"start": v(7.67, -15.88) * mm, "end": v(7.7, -21.49) * mm});
            skLineSegment(sketch, "E103", {"start": v(8.33, -23.42) * mm, "end": v(13.33, -23.42) * mm});
            skLineSegment(sketch, "E104", {"start": v(15.33, -23.42) * mm, "end": v(20.33, -23.42) * mm});
            skLineSegment(sketch, "E105", {"start": v(22.33, -23.42) * mm, "end": v(27.33, -23.42) * mm});
            skLineSegment(sketch, "E106", {"start": v(29.33, -23.42) * mm, "end": v(34.33, -23.42) * mm});
            skLineSegment(sketch, "E107", {"start": v(36.33, -23.42) * mm, "end": v(41.33, -23.42) * mm});
            skLineSegment(sketch, "E108", {"start": v(43.33, -23.42) * mm, "end": v(48.33, -23.42) * mm});
            skLineSegment(sketch, "E109", {"start": v(50.49, -23.38) * mm, "end": v(55.33, -23.42) * mm});
            skLineSegment(sketch, "E110", {"start": v(57.36, -23.37) * mm, "end": v(62.36, -23.47) * mm});
            skLineSegment(sketch, "E111", {"start": v(64.33, -23.42) * mm, "end": v(69.33, -23.42) * mm});
            skLineSegment(sketch, "E112", {"start": v(71.3, -23.47) * mm, "end": v(76.3, -23.37) * mm});
            skLineSegment(sketch, "E113", {"start": v(78.33, -23.42) * mm, "end": v(83.33, -23.42) * mm});
            skLineSegment(sketch, "E114", {"start": v(85.33, -23.42) * mm, "end": v(90.33, -23.42) * mm});
            skLineSegment(sketch, "E115", {"start": v(92.33, -23.42) * mm, "end": v(97.33, -23.42) * mm});
            skLineSegment(sketch, "E116", {"start": v(99.33, -23.42) * mm, "end": v(104.33, -23.42) * mm});
            skLineSegment(sketch, "E117", {"start": v(106.33, -23.42) * mm, "end": v(111.33, -23.42) * mm});
            skLineSegment(sketch, "E118", {"start": v(113.4, -23.46) * mm, "end": v(118.33, -23.42) * mm});
            skLineSegment(sketch, "E119", {"start": v(120.33, -23.42) * mm, "end": v(125.33, -23.42) * mm});
            skSolve(sketch);
        }
        {
            var Q0;
            Q0 = qSketchRegion(id + "F15", true);
            extrude(context, id + "F16", {"entities" : qUnion([Q0]), "operationType" : NewBodyOperationType.REMOVE, "oppositeDirection" : true, "depth" : 1 * mm});
        }
        {
            var Q0;
            Q0=makeQuery(id+"F14.opExtrude","SWEPT_BODY",BODY,{"disambiguationData":[OSD([sQuery(id+"F11.wireOp",EDGE,"E8.bottom"),sQuery(id+"F11.wireOp",EDGE,"E8.top"),sQuery(id+"F11.wireOp",EDGE,"E8.left"),sQuery(id+"F11.wireOp",EDGE,"E8.right")])]});
            transform(context, id + "F17", {"entities" : qUnion([Q0]), "transformType" : TransformType.TRANSLATION_3D, "dx" : 185 * mm, "dy" : 0 * mm, "dz" : 0 * mm, "makeCopy" : true});
        }
        {
            var Q0;
            Q0=makeQuery(id+"F3.opExtrude","CAP_FACE",FACE,{"disambiguationData":[OSD([sQuery(id+"F2.wireOp",EDGE,"E3.0"),sQuery(id+"F2.wireOp",EDGE,"E3.1"),sQuery(id+"F2.wireOp",EDGE,"E3.2"),sQuery(id+"F2.wireOp",EDGE,"E3.3"),sQuery(id+"F2.wireOp",EDGE,"E3.4"),sQuery(id+"F2.wireOp",EDGE,"E3.5")])],"isStart":false});
            var sketch = newSketch(context, id + "F18", { "sketchPlane" : qUnion([Q0])});
            skLineSegment(sketch, "E120.bottom", {"start": v(145.4, 9.9) * mm, "end": v(147.9, 9.9) * mm});
            skLineSegment(sketch, "E120.top", {"start": v(145.4, -12.1) * mm, "end": v(147.9, -12.1) * mm});
            skLineSegment(sketch, "E120.left", {"start": v(145.4, 9.9) * mm, "end": v(145.4, -12.1) * mm});
            skLineSegment(sketch, "E120.right", {"start": v(147.9, 9.9) * mm, "end": v(147.9, -12.1) * mm});
            skLineSegment(sketch, "E121", {"start": v(145.4, -12.1) * mm, "end": v(145.4, -12.1) * mm});
            skPoint(sketch, "E121.endSnap0", {"position": v(146.64, -12.1) * mm});
            skLineSegment(sketch, "E122.bottom", {"start": v(150.4, -12.06) * mm, "end": v(152.9, -12.06) * mm});
            skLineSegment(sketch, "E122.top", {"start": v(150.4, 3.94) * mm, "end": v(152.9, 3.94) * mm});
            skLineSegment(sketch, "E122.left", {"start": v(150.4, -12.06) * mm, "end": v(150.4, 3.94) * mm});
            skLineSegment(sketch, "E122.right", {"start": v(152.9, -12.06) * mm, "end": v(152.9, 3.94) * mm});
            skLineSegment(sketch, "E123.bottom", {"start": v(155.4, -12.03) * mm, "end": v(157.9, -12.03) * mm});
            skLineSegment(sketch, "E123.top", {"start": v(155.4, 6.97) * mm, "end": v(157.9, 6.97) * mm});
            skLineSegment(sketch, "E123.left", {"start": v(155.4, -12.03) * mm, "end": v(155.4, 6.97) * mm});
            skLineSegment(sketch, "E123.right", {"start": v(157.9, -12.03) * mm, "end": v(157.9, 6.97) * mm});
            skLineSegment(sketch, "E124.bottom", {"start": v(160.4, -12) * mm, "end": v(162.9, -12) * mm});
            skLineSegment(sketch, "E124.top", {"start": v(160.4, 0) * mm, "end": v(162.9, 0) * mm});
            skLineSegment(sketch, "E124.left", {"start": v(160.4, -12) * mm, "end": v(160.4, 0) * mm});
            skLineSegment(sketch, "E124.right", {"start": v(162.9, -12) * mm, "end": v(162.9, 0) * mm});
            skLineSegment(sketch, "E125.bottom", {"start": v(165.4, -11.97) * mm, "end": v(167.9, -11.97) * mm});
            skLineSegment(sketch, "E125.top", {"start": v(165.4, 15.53) * mm, "end": v(167.9, 15.53) * mm});
            skLineSegment(sketch, "E125.left", {"start": v(165.4, -11.97) * mm, "end": v(165.4, 15.53) * mm});
            skLineSegment(sketch, "E125.right", {"start": v(167.9, -11.97) * mm, "end": v(167.9, 15.53) * mm});
            skLineSegment(sketch, "E126.bottom", {"start": v(170.4, -11.94) * mm, "end": v(172.9, -11.94) * mm});
            skLineSegment(sketch, "E126.top", {"start": v(170.4, 5.06) * mm, "end": v(172.9, 5.06) * mm});
            skLineSegment(sketch, "E126.left", {"start": v(170.4, -11.94) * mm, "end": v(170.4, 5.06) * mm});
            skLineSegment(sketch, "E126.right", {"start": v(172.9, -11.94) * mm, "end": v(172.9, 5.06) * mm});
            skSolve(sketch);
        }
        {
            var Q0;
            Q0=makeQuery(id+"F18.imprint","IMPRINT",FACE,{"disambiguationData":[TD([[makeQuery(id+"F18.imprint","IMPRINT",EDGE,{"derivedFrom":sQuery(id+"F18.wireOp",EDGE,"E120.bottom")}),-1.0]])]});
            var Q1;
            Q1=makeQuery(id+"F18.imprint","IMPRINT",FACE,{"disambiguationData":[TD([[makeQuery(id+"F18.imprint","IMPRINT",EDGE,{"derivedFrom":sQuery(id+"F18.wireOp",EDGE,"E122.bottom")}),1.0]])]});
            var Q2;
            Q2=makeQuery(id+"F18.imprint","IMPRINT",FACE,{"disambiguationData":[TD([[makeQuery(id+"F18.imprint","IMPRINT",EDGE,{"derivedFrom":sQuery(id+"F18.wireOp",EDGE,"E123.bottom")}),1.0]])]});
            var Q3;
            Q3=makeQuery(id+"F18.imprint","IMPRINT",FACE,{"disambiguationData":[TD([[makeQuery(id+"F18.imprint","IMPRINT",EDGE,{"derivedFrom":sQuery(id+"F18.wireOp",EDGE,"E124.bottom")}),1.0]])]});
            var Q4;
            Q4=makeQuery(id+"F18.imprint","IMPRINT",FACE,{"disambiguationData":[TD([[makeQuery(id+"F18.imprint","IMPRINT",EDGE,{"derivedFrom":sQuery(id+"F18.wireOp",EDGE,"E125.bottom")}),1.0]])]});
            var Q5;
            Q5=makeQuery(id+"F18.imprint","IMPRINT",FACE,{"disambiguationData":[TD([[makeQuery(id+"F18.imprint","IMPRINT",EDGE,{"derivedFrom":sQuery(id+"F18.wireOp",EDGE,"E126.bottom")}),1.0]])]});
            extrude(context, id + "F19", {"entities" : qUnion([Q0, Q1, Q2, Q3, Q4, Q5]), "operationType" : NewBodyOperationType.REMOVE, "oppositeDirection" : true, "depth" : 2 * mm});
        }
        {
            var Q0;
            Q0=makeQuery(id+"F19.boolean.opBoolean","COPY",EDGE,{"derivedFrom":makeQuery(id+"F19.opExtrude","SWEPT_EDGE",EDGE,{"disambiguationData":[OSD([sQuery(id+"F18.wireOp",EDGE,"E120.bottom"),sQuery(id+"F18.wireOp",EDGE,"E120.left")])]})});
            var Q1;
            Q1=makeQuery(id+"F19.boolean.opBoolean","COPY",EDGE,{"derivedFrom":makeQuery(id+"F19.opExtrude","SWEPT_EDGE",EDGE,{"disambiguationData":[OSD([sQuery(id+"F18.wireOp",EDGE,"E120.bottom"),sQuery(id+"F18.wireOp",EDGE,"E120.right")])]})});
            var Q2;
            Q2=makeQuery(id+"F19.boolean.opBoolean","COPY",EDGE,{"derivedFrom":makeQuery(id+"F19.opExtrude","SWEPT_EDGE",EDGE,{"disambiguationData":[OSD([sQuery(id+"F18.wireOp",EDGE,"E120.top"),sQuery(id+"F18.wireOp",EDGE,"E120.left")])]})});
            var Q3;
            Q3=makeQuery(id+"F19.boolean.opBoolean","COPY",EDGE,{"derivedFrom":makeQuery(id+"F19.opExtrude","SWEPT_EDGE",EDGE,{"disambiguationData":[OSD([sQuery(id+"F18.wireOp",EDGE,"E120.top"),sQuery(id+"F18.wireOp",EDGE,"E120.right")])]})});
            var Q4;
            Q4=makeQuery(id+"F19.boolean.opBoolean","COPY",EDGE,{"derivedFrom":makeQuery(id+"F19.opExtrude","SWEPT_EDGE",EDGE,{"disambiguationData":[OSD([sQuery(id+"F18.wireOp",EDGE,"E122.top"),sQuery(id+"F18.wireOp",EDGE,"E122.left")])]})});
            var Q5;
            Q5=makeQuery(id+"F19.boolean.opBoolean","COPY",EDGE,{"derivedFrom":makeQuery(id+"F19.opExtrude","SWEPT_EDGE",EDGE,{"disambiguationData":[OSD([sQuery(id+"F18.wireOp",EDGE,"E122.top"),sQuery(id+"F18.wireOp",EDGE,"E122.right")])]})});
            var Q6;
            Q6=makeQuery(id+"F19.boolean.opBoolean","COPY",EDGE,{"derivedFrom":makeQuery(id+"F19.opExtrude","SWEPT_EDGE",EDGE,{"disambiguationData":[OSD([sQuery(id+"F18.wireOp",EDGE,"E122.bottom"),sQuery(id+"F18.wireOp",EDGE,"E122.right")])]})});
            var Q7;
            Q7=makeQuery(id+"F19.boolean.opBoolean","COPY",EDGE,{"derivedFrom":makeQuery(id+"F19.opExtrude","SWEPT_EDGE",EDGE,{"disambiguationData":[OSD([sQuery(id+"F18.wireOp",EDGE,"E122.bottom"),sQuery(id+"F18.wireOp",EDGE,"E122.left")])]})});
            var Q8;
            Q8=makeQuery(id+"F19.boolean.opBoolean","COPY",EDGE,{"derivedFrom":makeQuery(id+"F19.opExtrude","SWEPT_EDGE",EDGE,{"disambiguationData":[OSD([sQuery(id+"F18.wireOp",EDGE,"E123.top"),sQuery(id+"F18.wireOp",EDGE,"E123.left")])]})});
            var Q9;
            Q9=makeQuery(id+"F19.boolean.opBoolean","COPY",EDGE,{"derivedFrom":makeQuery(id+"F19.opExtrude","SWEPT_EDGE",EDGE,{"disambiguationData":[OSD([sQuery(id+"F18.wireOp",EDGE,"E123.top"),sQuery(id+"F18.wireOp",EDGE,"E123.right")])]})});
            var Q10;
            Q10=makeQuery(id+"F19.boolean.opBoolean","COPY",EDGE,{"derivedFrom":makeQuery(id+"F19.opExtrude","SWEPT_EDGE",EDGE,{"disambiguationData":[OSD([sQuery(id+"F18.wireOp",EDGE,"E123.bottom"),sQuery(id+"F18.wireOp",EDGE,"E123.right")])]})});
            var Q11;
            Q11=makeQuery(id+"F19.boolean.opBoolean","COPY",EDGE,{"derivedFrom":makeQuery(id+"F19.opExtrude","SWEPT_EDGE",EDGE,{"disambiguationData":[OSD([sQuery(id+"F18.wireOp",EDGE,"E123.bottom"),sQuery(id+"F18.wireOp",EDGE,"E123.left")])]})});
            var Q12;
            Q12=makeQuery(id+"F19.boolean.opBoolean","COPY",EDGE,{"derivedFrom":makeQuery(id+"F19.opExtrude","SWEPT_EDGE",EDGE,{"disambiguationData":[OSD([sQuery(id+"F18.wireOp",EDGE,"E124.top"),sQuery(id+"F18.wireOp",EDGE,"E124.left")])]})});
            var Q13;
            Q13=makeQuery(id+"F19.boolean.opBoolean","COPY",EDGE,{"derivedFrom":makeQuery(id+"F19.opExtrude","SWEPT_EDGE",EDGE,{"disambiguationData":[OSD([sQuery(id+"F18.wireOp",EDGE,"E124.top"),sQuery(id+"F18.wireOp",EDGE,"E124.right")])]})});
            var Q14;
            Q14=makeQuery(id+"F19.boolean.opBoolean","COPY",EDGE,{"derivedFrom":makeQuery(id+"F19.opExtrude","SWEPT_EDGE",EDGE,{"disambiguationData":[OSD([sQuery(id+"F18.wireOp",EDGE,"E124.bottom"),sQuery(id+"F18.wireOp",EDGE,"E124.right")])]})});
            var Q15;
            Q15=makeQuery(id+"F19.boolean.opBoolean","COPY",EDGE,{"derivedFrom":makeQuery(id+"F19.opExtrude","SWEPT_EDGE",EDGE,{"disambiguationData":[OSD([sQuery(id+"F18.wireOp",EDGE,"E124.bottom"),sQuery(id+"F18.wireOp",EDGE,"E124.left")])]})});
            var Q16;
            Q16=makeQuery(id+"F19.boolean.opBoolean","COPY",EDGE,{"derivedFrom":makeQuery(id+"F19.opExtrude","SWEPT_EDGE",EDGE,{"disambiguationData":[OSD([sQuery(id+"F18.wireOp",EDGE,"E125.top"),sQuery(id+"F18.wireOp",EDGE,"E125.left")])]})});
            var Q17;
            Q17=makeQuery(id+"F19.boolean.opBoolean","COPY",EDGE,{"derivedFrom":makeQuery(id+"F19.opExtrude","SWEPT_EDGE",EDGE,{"disambiguationData":[OSD([sQuery(id+"F18.wireOp",EDGE,"E125.top"),sQuery(id+"F18.wireOp",EDGE,"E125.right")])]})});
            var Q18;
            Q18=makeQuery(id+"F19.boolean.opBoolean","COPY",EDGE,{"derivedFrom":makeQuery(id+"F19.opExtrude","SWEPT_EDGE",EDGE,{"disambiguationData":[OSD([sQuery(id+"F18.wireOp",EDGE,"E125.bottom"),sQuery(id+"F18.wireOp",EDGE,"E125.right")])]})});
            var Q19;
            Q19=makeQuery(id+"F19.boolean.opBoolean","COPY",EDGE,{"derivedFrom":makeQuery(id+"F19.opExtrude","SWEPT_EDGE",EDGE,{"disambiguationData":[OSD([sQuery(id+"F18.wireOp",EDGE,"E125.bottom"),sQuery(id+"F18.wireOp",EDGE,"E125.left")])]})});
            var Q20;
            Q20=makeQuery(id+"F19.boolean.opBoolean","COPY",EDGE,{"derivedFrom":makeQuery(id+"F19.opExtrude","SWEPT_EDGE",EDGE,{"disambiguationData":[OSD([sQuery(id+"F18.wireOp",EDGE,"E126.top"),sQuery(id+"F18.wireOp",EDGE,"E126.right")])]})});
            var Q21;
            Q21=makeQuery(id+"F19.boolean.opBoolean","COPY",EDGE,{"derivedFrom":makeQuery(id+"F19.opExtrude","SWEPT_EDGE",EDGE,{"disambiguationData":[OSD([sQuery(id+"F18.wireOp",EDGE,"E126.top"),sQuery(id+"F18.wireOp",EDGE,"E126.left")])]})});
            var Q22;
            Q22=makeQuery(id+"F19.boolean.opBoolean","COPY",EDGE,{"derivedFrom":makeQuery(id+"F19.opExtrude","SWEPT_EDGE",EDGE,{"disambiguationData":[OSD([sQuery(id+"F18.wireOp",EDGE,"E126.bottom"),sQuery(id+"F18.wireOp",EDGE,"E126.right")])]})});
            var Q23;
            Q23=makeQuery(id+"F19.boolean.opBoolean","COPY",EDGE,{"derivedFrom":makeQuery(id+"F19.opExtrude","SWEPT_EDGE",EDGE,{"disambiguationData":[OSD([sQuery(id+"F18.wireOp",EDGE,"E126.bottom"),sQuery(id+"F18.wireOp",EDGE,"E126.left")])]})});
            fillet(context, id + "F20", {"entities" : qUnion([Q0, Q1, Q2, Q3, Q4, Q5, Q6, Q7, Q8, Q9, Q10, Q11, Q12, Q13, Q14, Q15, Q16, Q17, Q18, Q19, Q20, Q21, Q22, Q23]), "radius" : 1 * mm, "tangentPropagation" : true, "allowEdgeOverflow" : false});
        }
    });
